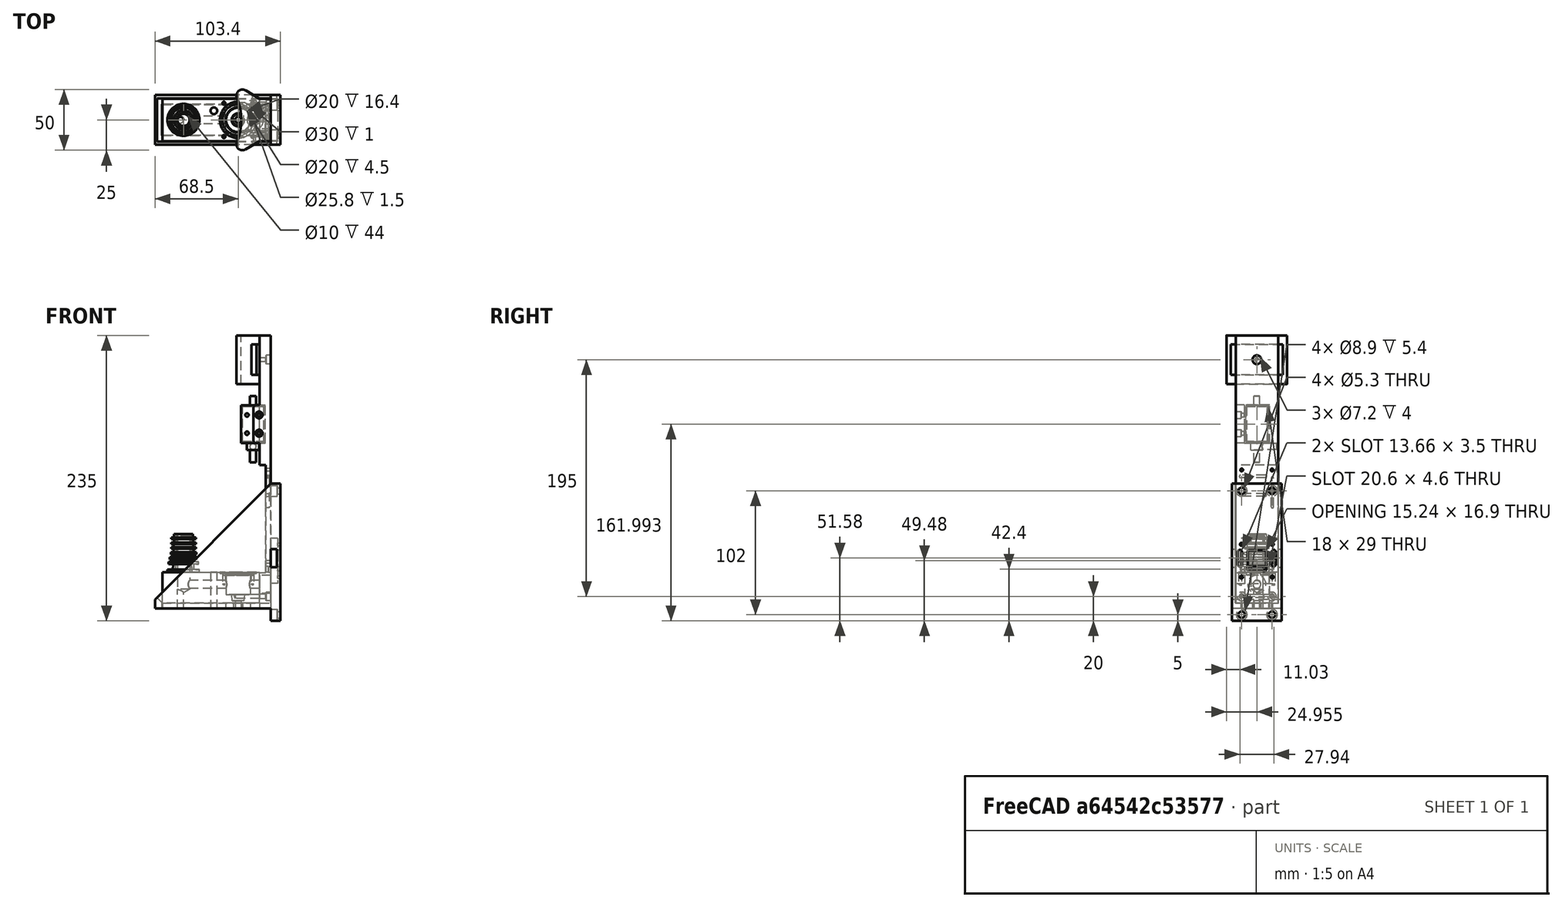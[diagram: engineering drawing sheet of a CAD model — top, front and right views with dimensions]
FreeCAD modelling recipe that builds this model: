
FCSTD DOCUMENT  (FreeCAD 1.0R39109 (Git))
Label: Bottle Nozzle V6.1
License: All rights reserved
LicenseURL: http://en.wikipedia.org/wiki/All_rights_reserved
objects: Sketcher::SketchObject×31, PartDesign::Pocket×12, PartDesign::Hole×10, PartDesign::Pad×6, Mesh::Feature×5, PartDesign::Body×4, TechDraw::DrawProjGroupItem×3, TechDraw::DrawViewDimension×3, PartDesign::Revolution×2, Spreadsheet::Sheet×1, PartDesign::Groove×1, TechDraw::DrawSVGTemplate×1, TechDraw::DrawPage×1, Part::FeaturePython×1
note: 160 computed .brp shape members not serialized (recipe doc carries the construction recipe); baked Part::Feature solids carry a one-line shape summary decoded from their .brp

FEATURE [Sketcher::SketchObject] Sketch
  ArcFitTolerance = 0
  FullyConstrained = true
  MakeInternals = false
  MapMode = 5
  Placement = pos=(0,0,0) rot=(1,0,0;1.5708rad)
  expr: Constraints[10] = Spreadsheet.HeightPart
  expr: Constraints[12] = Spreadsheet.PartWidth / 2
  expr: Constraints[13] = Spreadsheet.PipeCircle / 2
  expr: Constraints[17] = Spreadsheet.HeigthDop
  expr: Constraints[8] = Spreadsheet.PartWidth2 / 2
  sketch-geometry (8):
    g0: LineSegment StartX=6 StartY=60 StartZ=0 EndX=6.75 EndY=30 EndZ=0
    g1: LineSegment [constr] StartX=6.75 StartY=30 StartZ=0 EndX=17.5 EndY=30 EndZ=0
    g2: LineSegment [constr] StartX=17.5 StartY=30 StartZ=0 EndX=17.5 EndY=0 EndZ=0
    g3: LineSegment [constr] StartX=17.5 StartY=0 StartZ=0 EndX=0 EndY=0 EndZ=0
    g4: LineSegment StartX=0 StartY=60 StartZ=0 EndX=6 EndY=60 EndZ=0
    g5: LineSegment [constr] StartX=0 StartY=60 StartZ=0 EndX=0 EndY=0 EndZ=0
    g6: LineSegment StartX=6.75 StartY=30 StartZ=0 EndX=0 EndY=30 EndZ=0
    g7: LineSegment StartX=0 StartY=30 StartZ=0 EndX=0 EndY=60 EndZ=0
  constraints (23):
    c: Coincident(g0,g1)
    c: Coincident(g1,g2)
    c: Vertical(g2)
    c: Coincident(g2,g3)
    c: Horizontal(g3)
    c: Coincident(g4,g0)
    c: Horizontal(g4)
    c: Horizontal(g1)
    c: DistanceX(g-1,g0) = 6.75
    c: Coincident(g5,g4)
    c: DistanceY(g2,g2) = 30
    c: Vertical(g5)
    c: DistanceX(g-1,g0) = 6
    c: DistanceX(g-1,g2) = 17.5
    c: Coincident(g3,g5)
    c: PointOnObject(g-1,g3)
    c: PointOnObject(g-1,g5)
    c: DistanceY(g1,g0) = 30
    c: Coincident(g6,g0)
    c: PointOnObject(g6,g5)
    c: Horizontal(g6)
    c: Coincident(g7,g6)
    c: Coincident(g7,g4)
FEATURE [PartDesign::Revolution] Revolution
  Angle = 360
  Angle2 = 60
  Axis = (0,2e-16,1)
  Base = (0,0,0)
  Placement = pos=(0,0,0) rot=(1,0,0;1.5708rad)
  Profile = -> Sketch
  ReferenceAxis = -> Sketch [V_Axis]
  Reversed = true
  Suppressed = false
  Type = 0
FEATURE [Spreadsheet::Sheet] Spreadsheet
  cells = A1='DiameterTube; B1(DiameterTube)==5 mm; C1==(B1 / 2) ^ 2 * pi; E1='Outer available; F1==C4 - C1; G1='Similair to inner tube; H1==sqrt(F1 / pi); A2='TubeOffset; B2(TubeOffset)==2.5 mm; C2==(HeightPart - DiameterTube) / 2; A3='DiameterTubeInner; B3(DiameterTubeInner)==B1 - 2 mm; C3==(B3 / 2) ^ 2 * pi; E3='Inner available; F3==C3; H3==sqrt(F3 / pi); A4='DiameterHole; B4(DiameterHole)==10 mm; C4==(B4 / 2) ^ 2 * pi; D4='Max = PartWidth-Walls*2; E4='Ratio liquid VS air surface; F4==F1 / F3; A5='PipeCircle; B5(PipeCircle)==35 mm; A6='HeightPart; B6(HeightPart)==30 mm; A7='HeigthDop; B7(HeigthDop)==30 mm; A8='PartWidth; B8(PartWidth)==12 mm; A9='PartWidth2; B9(PartWidth2)==13.5 mm; A10='MountingHoleDistance; B10(MountingHoleDistance)==round(sqrt((((PipeCircle - PartWidth2) / 2 + PartWidth2) / 2) ^ 2 * 2) / 2.5) * 2.5; A11='OffsetFluidHole2; B11(OffsetFluidHole2)==OffsetFlakte - (4 mm + 0.8 mm * 8 / 2); C11='Blindstop Depth is 3mm+1mm spacer, M5 = 4.2mm; A12='WidthFlank; B12(WidthFlank)==10 mm; A13='OffsetFlakte; B13(OffsetFlakte)==sqrt(PipeCircle ^ 2 - (WidthFlank / 2) ^ 2) / 2 - 0.82 mm; A14='FluidHole; B14(FluidHole)==5 mm; C14='M7; A15='FluidHoleOutsideTube; B15(FluidHoleOutsideTube)==FluidHole + 2 mm; A16='PartOffset; B16(PartOffset)=10; A17='offsetvalve; B17(offsetvalve)=45
FEATURE [Sketcher::SketchObject] Sketch003
  ArcFitTolerance = 0
  AttachmentOffset = pos=(0,0,60) rot=(0,0,1;0rad)
  FullyConstrained = true
  MakeInternals = false
  MapMode = 5
  Placement = pos=(0,0,60) rot=(0,0,1;0rad)
  expr: .AttachmentOffset.Base.z = Spreadsheet.HeightPart + Spreadsheet.HeigthDop
  expr: Constraints[1] = Spreadsheet.DiameterHole
  sketch-geometry (1):
    g0: Circle CenterX=0 CenterY=0 CenterZ=0 NormalX=0 NormalY=0 NormalZ=1 AngleXU=0 Radius=5
  constraints (2):
    c: Coincident(g0,g-1)
    c: Diameter(g0) = 10
FEATURE [Sketcher::SketchObject] Sketch005
  ArcFitTolerance = 0
  FullyConstrained = true
  MakeInternals = false
  MapMode = 5
  expr: Constraints[0] = Spreadsheet.DiameterTube
  expr: Constraints[2] = Spreadsheet.TubeOffset
  sketch-geometry (1):
    g0: Circle CenterX=-2.5 CenterY=0 CenterZ=0 NormalX=0 NormalY=0 NormalZ=1 AngleXU=0 Radius=2.5
  constraints (3):
    c: Diameter(g0) = 5
    c: PointOnObject(g0,g-1)
    c: DistanceX(g0,g-1) = 2.5
FEATURE [Sketcher::SketchObject] Sketch006
  ArcFitTolerance = 0
  FullyConstrained = true
  MakeInternals = false
  MapMode = 5
  expr: Constraints[18] = Spreadsheet.PipeCircle / 2
  expr: Constraints[9] = Spreadsheet.PipeCircle
  sketch-geometry (7):
    g0: LineSegment StartX=0 StartY=17.5 StartZ=0 EndX=62.5 EndY=17.5 EndZ=0
    g1: LineSegment StartX=62.5 StartY=17.5 StartZ=0 EndX=62.5 EndY=-17.5 EndZ=0
    g2: LineSegment StartX=62.5 StartY=-17.5 StartZ=0 EndX=0 EndY=-17.5 EndZ=0
    g3: LineSegment [constr] StartX=0 StartY=-17.5 StartZ=0 EndX=0 EndY=17.5 EndZ=0
    g4: LineSegment StartX=0 StartY=17.5 StartZ=0 EndX=-17.5 EndY=17.5 EndZ=0
    g5: LineSegment StartX=-17.5 StartY=17.5 StartZ=0 EndX=-17.5 EndY=-17.5 EndZ=0
    g6: LineSegment StartX=-17.5 StartY=-17.5 StartZ=0 EndX=0 EndY=-17.5 EndZ=0
  constraints (19):
    c: Coincident(g0,g1)
    c: Coincident(g1,g2)
    c: Coincident(g2,g3)
    c: Coincident(g3,g0)
    c: Horizontal(g0)
    c: Horizontal(g2)
    c: Vertical(g1)
    c: PointOnObject(g0,g-2)
    c: Symmetric(g0,g2,g-1)
    c: DistanceY(g3,g3) = 35
    c: DistanceX(g0,g0) = 62.5  'ww'
    c: Coincident(g0,g4)
    c: Horizontal(g4)
    c: Coincident(g4,g5)
    c: Vertical(g5)
    c: Coincident(g5,g6)
    c: Coincident(g6,g2)
    c: Horizontal(g6)
    c: DistanceX(g4,g4) = 17.5
FEATURE [PartDesign::Pad] Pad
  BaseFeature = -> Revolution
  Direction = (0,0,1)
  Length = 30
  Length2 = 10
  Placement = pos=(0,0,0) rot=(1,0,0;1.5708rad)
  Profile = -> Sketch006
  ReferenceAxis = -> Sketch006 [N_Axis]
  Suppressed = false
  Type = 0
  expr: Length = Spreadsheet.HeightPart
FEATURE [PartDesign::Hole] Hole  label="Hole Combination"
  BaseFeature = -> Pad
  CustomThreadClearance = 0
  Depth = 44
  DepthType = 0
  Diameter = 10
  DrillForDepth = false
  DrillPoint = 1
  DrillPointAngle = 118
  HoleCutCountersinkAngle = 90
  HoleCutCustomValues = false
  HoleCutDepth = 0
  HoleCutDiameter = 10.1
  HoleCutType = 0
  ModelThread = false
  Placement = pos=(0,0,0) rot=(1,0,0;1.5708rad)
  Profile = -> Sketch003
  Suppressed = false
  Tapered = false
  TaperedAngle = 90
  ThreadClass = 0
  ThreadDepth = 44
  ThreadDepthType = 0
  ThreadDirection = 0
  ThreadFit = 0
  ThreadSize = 0
  ThreadType = 0
  Threaded = false
  UseCustomThreadClearance = false
  expr: Depth = 44 mm
FEATURE [PartDesign::Hole] Hole001  label="Hole Air"
  BaseFeature = -> Hole
  CustomThreadClearance = 0
  Depth = 210.228
  DepthType = 1
  Diameter = 5
  DrillForDepth = false
  DrillPoint = 1
  DrillPointAngle = 118
  HoleCutCountersinkAngle = 90
  HoleCutCustomValues = false
  HoleCutDepth = 0
  HoleCutDiameter = 6.1
  HoleCutType = 0
  ModelThread = false
  Placement = pos=(0,0,0) rot=(1,0,0;1.5708rad)
  Profile = -> Sketch005
  Reversed = true
  Suppressed = false
  Tapered = false
  TaperedAngle = 90
  ThreadClass = 0
  ThreadDepth = 210.228
  ThreadDepthType = 0
  ThreadDirection = 0
  ThreadFit = 0
  ThreadSize = 0
  ThreadType = 0
  Threaded = false
  UseCustomThreadClearance = false
FEATURE [Sketcher::SketchObject] Sketch011
  ArcFitTolerance = 0
  AttachmentOffset = pos=(0,0,62.5) rot=(0,0,1;0rad)
  FullyConstrained = true
  MakeInternals = false
  MapMode = 5
  Placement = pos=(62.5,0,0) rot=(0.57735,0.57735,0.57735;2.0944rad)
  expr: .AttachmentOffset.Base.z = Sketch006.Constraints.ww
  expr: .Constraints.hh = 20
  sketch-geometry (1):
    g0: Circle CenterX=0 CenterY=20 CenterZ=0 NormalX=0 NormalY=0 NormalZ=1 AngleXU=0 Radius=4
  constraints (3):
    c: PointOnObject(g0,g-2)
    c: Diameter(g0) = 8
    c: DistanceY(g-1,g0) = 20  'hh'
FEATURE [PartDesign::Hole] Hole002  label="Hole Side"
  BaseFeature = -> Hole001
  CustomThreadClearance = 0
  Depth = 60
  DepthType = 0
  Diameter = 6.4
  DrillForDepth = false
  DrillPoint = 1
  DrillPointAngle = 118
  HoleCutCountersinkAngle = 90
  HoleCutCustomValues = false
  HoleCutDepth = 0
  HoleCutDiameter = 0
  HoleCutType = 0
  ModelThread = false
  Placement = pos=(0,0,0) rot=(1,0,0;1.5708rad)
  Profile = -> Sketch011
  Suppressed = false
  Tapered = false
  TaperedAngle = 90
  ThreadClass = 0
  ThreadDepth = 60
  ThreadDepthType = 0
  ThreadDirection = 0
  ThreadFit = 0
  ThreadSize = 0
  ThreadType = 0
  Threaded = false
  UseCustomThreadClearance = false
  expr: Diameter = 8 * 0.8
FEATURE [Sketcher::SketchObject] Sketch012
  ArcFitTolerance = 0
  AttachmentOffset = pos=(0,0,45) rot=(0,0,1;0rad)
  FullyConstrained = true
  MakeInternals = false
  MapMode = 5
  Placement = pos=(45,0,0) rot=(0.57735,0.57735,0.57735;2.0944rad)
  expr: .AttachmentOffset.Base.z = Spreadsheet.offsetvalve
  expr: Constraints[13] = 25.8 / 2
  expr: Constraints[17] = 20 / 2
  expr: Constraints[24] = 10.8 / 2
  expr: Constraints[25] = 8.6 / 2
  sketch-geometry (15):
    g0: LineSegment StartX=15 StartY=30 StartZ=0 EndX=15 EndY=29 EndZ=0
    g1: LineSegment StartX=15 StartY=29 StartZ=0 EndX=12.9 EndY=29 EndZ=0
    g2: LineSegment StartX=12.9 StartY=29 StartZ=0 EndX=12.9 EndY=27.5 EndZ=0
    g3: LineSegment StartX=12.9 StartY=27.5 StartZ=0 EndX=10.4 EndY=27.5 EndZ=0
    g4: LineSegment StartX=10.4 StartY=27.5 StartZ=0 EndX=10.4 EndY=27.9 EndZ=0
    g5: LineSegment StartX=10 StartY=27.9 StartZ=0 EndX=10 EndY=11.5 EndZ=0
    g6: LineSegment StartX=10 StartY=27.9 StartZ=0 EndX=10.4 EndY=27.9 EndZ=0
    g7: LineSegment StartX=10 StartY=11.5 StartZ=0 EndX=5.4 EndY=11.5 EndZ=0
    g8: LineSegment [constr] StartX=5.4 StartY=11.5 StartZ=0 EndX=4.3 EndY=2.5 EndZ=0
    g9: LineSegment StartX=0 StartY=30 StartZ=0 EndX=0 EndY=0 EndZ=0
    g10: LineSegment StartX=15 StartY=30 StartZ=0 EndX=0 EndY=30 EndZ=0
    g11: LineSegment StartX=2.5 StartY=6.5 StartZ=0 EndX=2.5 EndY=0 EndZ=0
    g12: LineSegment StartX=0 StartY=0 StartZ=0 EndX=2.5 EndY=0 EndZ=0
    g13: LineSegment StartX=5.4 StartY=11.5 StartZ=0 EndX=4.78889 EndY=6.5 EndZ=0
    g14: LineSegment StartX=4.78889 StartY=6.5 StartZ=0 EndX=2.5 EndY=6.5 EndZ=0
  constraints (45):
    c: Vertical(g0)
    c: DistanceY(g-1,g0) = 30
    c: Coincident(g0,g1)
    c: Horizontal(g1)
    c: Coincident(g1,g2)
    c: Vertical(g2)
    c: Coincident(g2,g3)
    c: Coincident(g3,g4)
    c: Vertical(g4)
    c: Vertical(g5)
    c: Horizontal(g3)
    c: DistanceY(g0,g0) = 1
    c: DistanceY(g2,g2) = 1.5
    c: DistanceX(g-1,g1) = 12.9
    c: Coincident(g6,g5)
    c: Coincident(g6,g4)
    c: Horizontal(g6)
    c: DistanceX(g-1,g5) = 10
    c: DistanceY(g4,g4) = 0.4
    c: Equal(g4,g6)
    c: Coincident(g5,g7)
    c: Coincident(g7,g8)
    c: PointOnObject(g9,g-2)
    c: Horizontal(g7)
    c: DistanceX(g-1,g7) = 5.4
    c: DistanceX(g-1,g8) = 4.3
    c: DistanceY(g8,g8) = 9
    c: DistanceY(g5,g3) = 16
    c: DistanceX(g-1,g0) = 15
    c: Coincident(g10,g0)
    c: Coincident(g10,g9)
    c: Horizontal(g10)
    c: DistanceX(g9,g11) = 2.5
    c: PointOnObject(g9,g-2)
    c: PointOnObject(g9,g-1)
    c: PointOnObject(g11,g-1)
    c: Vertical(g11)
    c: Coincident(g12,g9)
    c: Coincident(g12,g11)
    c: Coincident(g13,g7)
    c: PointOnObject(g13,g8)
    c: Coincident(g14,g13)
    c: Horizontal(g14)
    c: DistanceY(g13,g13) = 5
    c: Coincident(g11,g14)
FEATURE [PartDesign::Groove] Groove  label="Groove valve"
  Angle = 360
  Angle2 = 60
  Axis = (1e-16,-1e-16,1)
  Base = (45,0,0)
  BaseFeature = -> Hole002
  Placement = pos=(0,0,0) rot=(1,0,0;1.5708rad)
  Profile = -> Sketch012
  ReferenceAxis = -> Sketch012 [V_Axis]
  Suppressed = false
  Type = 0
FEATURE [Sketcher::SketchObject] Sketch013
  ArcFitTolerance = 0
  AttachmentOffset = pos=(0,0,30) rot=(0,0,1;0rad)
  FullyConstrained = true
  MakeInternals = false
  MapMode = 5
  Placement = pos=(0,0,30) rot=(0,0,1;0rad)
  expr: .AttachmentOffset.Base.z = Spreadsheet.HeightPart
  expr: Constraints[10] = Spreadsheet.offsetvalve
  sketch-geometry (9):
    g0: LineSegment [constr] StartX=33.25 StartY=-13.75 StartZ=0 EndX=33.25 EndY=13.75 EndZ=0
    g1: LineSegment [constr] StartX=33.25 StartY=13.75 StartZ=0 EndX=56.75 EndY=13.75 EndZ=0
    g2: LineSegment [constr] StartX=56.75 StartY=13.75 StartZ=0 EndX=56.75 EndY=-13.75 EndZ=0
    g3: LineSegment [constr] StartX=56.75 StartY=-13.75 StartZ=0 EndX=33.25 EndY=-13.75 EndZ=0
    g4: GeomPoint X=45 Y=-6e-16 Z=0
    g5: Circle CenterX=33.25 CenterY=13.75 CenterZ=0 NormalX=0 NormalY=0 NormalZ=1 AngleXU=0 Radius=1.75
    g6: Circle CenterX=56.75 CenterY=13.75 CenterZ=0 NormalX=0 NormalY=0 NormalZ=1 AngleXU=0 Radius=1.75
    g7: Circle CenterX=33.25 CenterY=-13.75 CenterZ=0 NormalX=0 NormalY=0 NormalZ=1 AngleXU=0 Radius=1.75
    g8: Circle CenterX=56.75 CenterY=-13.75 CenterZ=0 NormalX=0 NormalY=0 NormalZ=1 AngleXU=0 Radius=1.75
  constraints (21):
    c: Coincident(g0,g1)
    c: Coincident(g1,g2)
    c: Coincident(g2,g3)
    c: Coincident(g3,g0)
    c: Horizontal(g1)
    c: Horizontal(g3)
    c: Vertical(g0)
    c: Vertical(g2)
    c: Symmetric(g1,g0,g4)
    c: PointOnObject(g4,g-1)
    c: DistanceX(g-1,g4) = 45
    c: Coincident(g5,g0)
    c: DistanceX(g1,g1) = 23.5
    c: DistanceY(g2,g2) = 27.5
    c: Coincident(g6,g1)
    c: Coincident(g7,g0)
    c: Coincident(g8,g2)
    c: Equal(g5,g6)
    c: Equal(g6,g7)
    c: Equal(g7,g8)
    c: Diameter(g6) = 3.5
FEATURE [PartDesign::Hole] Hole003  label="Hole mouting valve thread"
  BaseFeature = -> Groove
  CustomThreadClearance = 0
  Depth = 10
  DepthType = 0
  Diameter = 2.5
  DrillForDepth = false
  DrillPoint = 1
  DrillPointAngle = 118
  HoleCutCountersinkAngle = 90
  HoleCutCustomValues = false
  HoleCutDepth = 0
  HoleCutDiameter = 6.1
  HoleCutType = 0
  ModelThread = false
  Placement = pos=(0,0,0) rot=(1,0,0;1.5708rad)
  Profile = -> Sketch013
  Suppressed = false
  Tapered = false
  TaperedAngle = 90
  ThreadClass = 0
  ThreadDepth = 10
  ThreadDepthType = 0
  ThreadDirection = 0
  ThreadFit = 0
  ThreadSize = 9
  ThreadType = 1
  Threaded = true
  UseCustomThreadClearance = false
FEATURE [Sketcher::SketchObject] Sketch014
  ArcFitTolerance = 0
  AttachmentOffset = pos=(0,0,62.5) rot=(0,0,1;0rad)
  FullyConstrained = false
  MakeInternals = false
  MapMode = 5
  Placement = pos=(62.5,0,0) rot=(0.57735,0.57735,0.57735;2.0944rad)
  expr: .AttachmentOffset.Base.z = Sketch006.Constraints.ww
  expr: Constraints[1] = Sketch011.Constraints.hh
  sketch-geometry (1):
    g0: Circle CenterX=0 CenterY=20 CenterZ=0 NormalX=0 NormalY=0 NormalZ=1 AngleXU=0 Radius=3.71689
  constraints (2):
    c: PointOnObject(g0,g-2)
    c: DistanceY(g-1,g0) = 20
FEATURE [PartDesign::Hole] Hole004  label="Hole Side thread"
  BaseFeature = -> Hole003
  CustomThreadClearance = 0
  Depth = 20
  DepthType = 0
  Diameter = 6.8
  DrillForDepth = false
  DrillPoint = 1
  DrillPointAngle = 118
  HoleCutCountersinkAngle = 90
  HoleCutCustomValues = false
  HoleCutDepth = 0
  HoleCutDiameter = 6.1
  HoleCutType = 0
  ModelThread = false
  Placement = pos=(0,0,0) rot=(1,0,0;1.5708rad)
  Profile = -> Sketch014
  Suppressed = false
  Tapered = false
  TaperedAngle = 90
  ThreadClass = 0
  ThreadDepth = 20
  ThreadDepthType = 0
  ThreadDirection = 0
  ThreadFit = 0
  ThreadSize = 16
  ThreadType = 1
  Threaded = true
  UseCustomThreadClearance = false
FEATURE [Sketcher::SketchObject] Sketch015
  ArcFitTolerance = 0
  AttachmentOffset = pos=(0,0,4.5) rot=(0,0,1;0rad)
  FullyConstrained = true
  MakeInternals = false
  MapMode = 5
  Placement = pos=(0,0,4.5) rot=(0,0,1;0rad)
  expr: Constraints[14] = Spreadsheet.PipeCircle
  expr: Constraints[15] = Sketch006.Constraints.ww
  expr: Constraints[2] = Spreadsheet.offsetvalve
  sketch-geometry (14):
    g0: Circle CenterX=45 CenterY=0 CenterZ=0 NormalX=0 NormalY=0 NormalZ=1 AngleXU=0 Radius=10
    g1: Circle CenterX=45 CenterY=0 CenterZ=0 NormalX=0 NormalY=0 NormalZ=1 AngleXU=0 Radius=3.5
    g2: LineSegment [constr] StartX=0 StartY=17.5 StartZ=0 EndX=62.5 EndY=17.5 EndZ=0
    g3: LineSegment [constr] StartX=62.5 StartY=17.5 StartZ=0 EndX=62.5 EndY=-17.5 EndZ=0
    g4: LineSegment [constr] StartX=62.5 StartY=-17.5 StartZ=0 EndX=0 EndY=-17.5 EndZ=0
    g5: LineSegment [constr] StartX=0 StartY=-17.5 StartZ=0 EndX=0 EndY=17.5 EndZ=0
    g6: LineSegment StartX=62.5 StartY=17.5 StartZ=0 EndX=-50 EndY=17.5 EndZ=0
    g7: LineSegment StartX=-50 StartY=17.5 StartZ=0 EndX=-50 EndY=12.5 EndZ=0
    g8: LineSegment StartX=-50 StartY=12.5 StartZ=0 EndX=62.5 EndY=12.5 EndZ=0
    g9: LineSegment StartX=62.5 StartY=12.5 StartZ=0 EndX=62.5 EndY=17.5 EndZ=0
    g10: LineSegment StartX=62.5 StartY=-17.5 StartZ=0 EndX=-50 EndY=-17.5 EndZ=0
    g11: LineSegment StartX=-50 StartY=-17.5 StartZ=0 EndX=-50 EndY=-12.5 EndZ=0
    g12: LineSegment StartX=-50 StartY=-12.5 StartZ=0 EndX=62.5 EndY=-12.5 EndZ=0
    g13: LineSegment StartX=62.5 StartY=-12.5 StartZ=0 EndX=62.5 EndY=-17.5 EndZ=0
  constraints (38):
    c: PointOnObject(g0,g-1)
    c: Coincident(g1,g0)
    c: DistanceX(g-1,g0) = 45
    c: Diameter(g1) = 7
    c: Diameter(g0) = 20
    c: Coincident(g2,g3)
    c: Coincident(g3,g4)
    c: Coincident(g4,g5)
    c: Coincident(g5,g2)
    c: Horizontal(g2)
    c: Horizontal(g4)
    c: Vertical(g5)
    c: PointOnObject(g2,g-2)
    c: Symmetric(g2,g3,g-1)
    c: DistanceY(g3,g3) = 35
    c: DistanceX(g2,g2) = 62.5
    c: Coincident(g6,g7)
    c: Coincident(g7,g8)
    c: Coincident(g8,g9)
    c: Coincident(g9,g6)
    c: Horizontal(g6)
    c: Horizontal(g8)
    c: Vertical(g7)
    c: Vertical(g9)
    c: Coincident(g6,g2)
    c: Coincident(g10,g11)
    c: Coincident(g11,g12)
    c: Coincident(g12,g13)
    c: Coincident(g13,g10)
    c: Horizontal(g10)
    c: Horizontal(g12)
    c: Vertical(g11)
    c: Vertical(g13)
    c: Coincident(g10,g3)
    c: Vertical(g11,g7)
    c: DistanceY(g12,g8) = 25
    c: Equal(g7,g11)
    c: DistanceX(g6,g2) = 50
FEATURE [PartDesign::Pocket] Pocket001  label="Pocket fluid outlet pipe"
  BaseFeature = -> Hole004
  Direction = (0,0,-1)
  Length = 5
  Length2 = 5
  Placement = pos=(0,0,0) rot=(1,0,0;1.5708rad)
  Profile = -> Sketch015
  ReferenceAxis = -> Sketch015 [N_Axis]
  Suppressed = false
  Type = 0
FEATURE [Sketcher::SketchObject] Sketch016
  ArcFitTolerance = 0
  AttachmentOffset = pos=(0,0,62.5) rot=(0,0,1;0rad)
  FullyConstrained = false
  MakeInternals = false
  MapMode = 5
  Placement = pos=(62.5,0,0) rot=(0.57735,0.57735,0.57735;2.0944rad)
  sketch-geometry (9):
    g0: LineSegment [constr] StartX=-12.5 StartY=10 StartZ=0 EndX=12.5 EndY=10 EndZ=0
    g1: LineSegment [constr] StartX=12.5 StartY=10 StartZ=0 EndX=12.5 EndY=25 EndZ=0
    g2: LineSegment [constr] StartX=12.5 StartY=25 StartZ=0 EndX=-12.5 EndY=25 EndZ=0
    g3: LineSegment [constr] StartX=-12.5 StartY=25 StartZ=0 EndX=-12.5 EndY=10 EndZ=0
    g4: GeomPoint [constr] X=0 Y=17.5 Z=0
    g5: Circle [constr] CenterX=12.5 CenterY=25 CenterZ=0 NormalX=0 NormalY=0 NormalZ=1 AngleXU=0 Radius=2.9952
    g6: Circle [constr] CenterX=-12.5 CenterY=25 CenterZ=0 NormalX=0 NormalY=0 NormalZ=1 AngleXU=0 Radius=2.9952
    g7: Circle CenterX=-12.5 CenterY=10 CenterZ=0 NormalX=0 NormalY=0 NormalZ=1 AngleXU=0 Radius=2.9952
    g8: Circle CenterX=12.5 CenterY=10 CenterZ=0 NormalX=0 NormalY=0 NormalZ=1 AngleXU=0 Radius=2.9952
  constraints (20):
    c: Coincident(g0,g1)
    c: Coincident(g1,g2)
    c: Coincident(g2,g3)
    c: Coincident(g3,g0)
    c: Horizontal(g0)
    c: Horizontal(g2)
    c: Vertical(g1)
    c: Vertical(g3)
    c: Symmetric(g2,g0,g4)
    c: PointOnObject(g4,g-2)
    c: DistanceX(g2,g2) = 25
    c: DistanceY(g1,g1) = 15
    c: Coincident(g5,g1)
    c: Coincident(g6,g2)
    c: Coincident(g7,g0)
    c: Coincident(g8,g0)
    c: Equal(g5,g8)
    c: Equal(g8,g7)
    c: Equal(g7,g6)
    c: DistanceY(g-1,g0) = 10
FEATURE [PartDesign::Hole] Hole005  label="Hole bottle holder mounting"
  BaseFeature = -> Pocket001
  CustomThreadClearance = 0
  Depth = 20
  DepthType = 0
  Diameter = 3.2
  DrillForDepth = false
  DrillPoint = 1
  DrillPointAngle = 118
  HoleCutCountersinkAngle = 90
  HoleCutCustomValues = false
  HoleCutDepth = 0
  HoleCutDiameter = 6.1
  HoleCutType = 0
  ModelThread = false
  Placement = pos=(0,0,0) rot=(1,0,0;1.5708rad)
  Profile = -> Sketch016
  Refine = true
  Suppressed = false
  Tapered = false
  TaperedAngle = 90
  ThreadClass = 0
  ThreadDepth = 20
  ThreadDepthType = 0
  ThreadDirection = 0
  ThreadFit = 0
  ThreadSize = 0
  ThreadType = 0
  Threaded = false
  UseCustomThreadClearance = false
  expr: Diameter = 0.8 * 4
FEATURE [Sketcher::SketchObject] Sketch018
  ArcFitTolerance = 0
  FullyConstrained = true
  MakeInternals = false
  MapMode = 5
  Placement = pos=(0,0,0) rot=(1,0,0;1.5708rad)
  expr: .Constraints.width = 71.9
  sketch-geometry (15):
    g0: LineSegment StartX=71.9 StartY=102.9 StartZ=0 EndX=-23.5 EndY=7.5 EndZ=0
    g1: LineSegment StartX=-23.5 StartY=7.5 StartZ=0 EndX=-23.5 EndY=0 EndZ=0
    g2: LineSegment StartX=-23.5 StartY=0 StartZ=0 EndX=71.9 EndY=0 EndZ=0
    g3: LineSegment [constr] StartX=71.9 StartY=0 StartZ=0 EndX=71.9 EndY=102.9 EndZ=0
    g4: LineSegment StartX=71.9 StartY=0 StartZ=0 EndX=71.9 EndY=-10 EndZ=0
    g5: Circle [constr] CenterX=-20.7041 CenterY=3.75 CenterZ=0 NormalX=0 NormalY=0 NormalZ=1 AngleXU=0 Radius=1.6
    g6: LineSegment [constr] StartX=-23.5 StartY=7.5 StartZ=0 EndX=-20.5 EndY=7.5 EndZ=0
    g7: LineSegment [constr] StartX=-20.5 StartY=7.5 StartZ=0 EndX=-17.5 EndY=4.5 EndZ=0
    g8: LineSegment [constr] StartX=-23.5 StartY=0 StartZ=0 EndX=-20.7041 EndY=3.75 EndZ=0
    g9: LineSegment [constr] StartX=-20.7041 StartY=3.75 StartZ=0 EndX=-23.5 EndY=7.5 EndZ=0
    g10: LineSegment [constr] StartX=-23.5 StartY=3.75 StartZ=0 EndX=-22.3041 EndY=3.75 EndZ=0
    g11: LineSegment [constr] StartX=-18.727 StartY=5.72703 StartZ=0 EndX=-19.5727 EndY=4.88137 EndZ=0
    g12: LineSegment StartX=71.9 StartY=102.9 StartZ=0 EndX=79.9 EndY=102.9 EndZ=0
    g13: LineSegment StartX=79.9 StartY=102.9 StartZ=0 EndX=79.9 EndY=-10 EndZ=0
    g14: LineSegment StartX=71.9 StartY=-10 StartZ=0 EndX=79.9 EndY=-10 EndZ=0
  constraints (45):
    c: Coincident(g0,g1)
    c: Coincident(g1,g2)
    c: PointOnObject(g3,g-1)
    c: Vertical(g3)
    c: Vertical(g4)
    c: DistanceX(g1,g-1) = 23.5
    c: DistanceY(g1,g1) = 7.5
    c: DistanceX(g-1,g3) = 71.9  'width'
    c: PointOnObject(g-1,g2)
    c: Horizontal(g2)
    c: Vertical(g1)
    c: Coincident(g4,g2)
    c: Vertical(g0,g2)
    c: Angle(g2,g0) = 0.785398
    c: DistanceY(g4,g4) = 10  'MountingHeight'
    c: Diameter(g5) = 3.2
    c: Coincident(g6,g0)
    c: Horizontal(g6)
    c: Coincident(g7,g6)
    c: DistanceX(g6,g6) = 3
    c: DistanceX(g7,g7) = 3
    c: DistanceY(g7,g7) = 3
    c: Coincident(g8,g1)
    c: Coincident(g8,g5)
    c: Coincident(g9,g5)
    c: Coincident(g9,g0)
    c: Equal(g9,g8)
    c: PointOnObject(g10,g1)
    c: PointOnObject(g10,g5)
    c: Horizontal(g10)
    c: PointOnObject(g11,g7)
    c: PointOnObject(g11,g5)
    c: Perpendicular(g7,g11)
    c: Equal(g10,g11)
    c: PointOnObject(g5,g10)
    c: PointOnObject(g5,g11)
    c: Horizontal(g12)
    c: Distance(g12,g12) = 8
    c: Coincident(g12,g13)
    c: Vertical(g13)
    c: Coincident(g14,g4)
    c: Coincident(g14,g13)
    c: Horizontal(g14)
    c: Coincident(g0,g12)
    c: Coincident(g3,g0)
FEATURE [PartDesign::Pad] Pad001  label="Pad all"
  Direction = (0,-1,2e-16)
  Length = 41
  Length2 = 10
  Midplane = true
  Placement = pos=(0,0,0) rot=(1,0,0;1.5708rad)
  Profile = -> Sketch018
  ReferenceAxis = -> Sketch018 [N_Axis]
  Suppressed = false
  Type = 0
  expr: Length = 35 + 3 * 2
FEATURE [Sketcher::SketchObject] Sketch019
  ArcFitTolerance = 0
  FullyConstrained = true
  MakeInternals = false
  MapMode = 5
  Placement = pos=(0,0,0) rot=(1,0,0;1.5708rad)
  expr: Constraints[3] = Sketch018.Constraints.width
  sketch-geometry (5):
    g0: LineSegment StartX=-17.5 StartY=4.5 StartZ=0 EndX=71.9 EndY=4.5 EndZ=0
    g1: LineSegment StartX=71.9 StartY=4.5 StartZ=0 EndX=71.9 EndY=104.5 EndZ=0
    g2: LineSegment StartX=-17.5 StartY=4.5 StartZ=0 EndX=-27.5 EndY=14.5 EndZ=0
    g3: LineSegment StartX=-27.5 StartY=14.5 StartZ=0 EndX=-27.5 EndY=104.5 EndZ=0
    g4: LineSegment StartX=-27.5 StartY=104.5 StartZ=0 EndX=71.9 EndY=104.5 EndZ=0
  constraints (15):
    c: Horizontal(g0)
    c: Coincident(g0,g1)
    c: Vertical(g1)
    c: DistanceX(g-1,g1) = 71.9
    c: DistanceY(g-1,g0) = 4.5
    c: Coincident(g3,g2)
    c: Vertical(g3)
    c: DistanceX(g0,g-1) = 17.5
    c: Coincident(g4,g3)
    c: Coincident(g4,g1)
    c: Horizontal(g4)
    c: Angle(g0,g2) = 2.35619
    c: Coincident(g2,g0)
    c: DistanceX(g2,g2) = 10
    c: DistanceY(g1,g1) = 100
FEATURE [PartDesign::Pocket] Pocket  label="Pocket 1"
  BaseFeature = -> Pad001
  Direction = (0,1,-2e-16)
  Length = 35.6
  Length2 = 5
  Midplane = true
  Placement = pos=(0,0,0) rot=(1,0,0;1.5708rad)
  Profile = -> Sketch019
  ReferenceAxis = -> Sketch019 [N_Axis]
  Suppressed = false
  Type = 0
  expr: Length = 35 + 0.6
FEATURE [Sketcher::SketchObject] Sketch020
  ArcFitTolerance = 0
  FullyConstrained = true
  MakeInternals = false
  MapMode = 5
  Placement = pos=(0,0,0) rot=(1,0,0;1.5708rad)
  expr: Constraints[10] = 17.5 mm + 0.25 mm
  expr: Constraints[11] = Sketch018.Constraints.width
  sketch-geometry (4):
    g0: LineSegment StartX=-17.75 StartY=5 StartZ=0 EndX=71.9 EndY=5 EndZ=0
    g1: LineSegment StartX=71.9 StartY=5 StartZ=0 EndX=71.9 EndY=0 EndZ=0
    g2: LineSegment StartX=71.9 StartY=0 StartZ=0 EndX=-17.75 EndY=0 EndZ=0
    g3: LineSegment StartX=-17.75 StartY=0 StartZ=0 EndX=-17.75 EndY=5 EndZ=0
  constraints (12):
    c: Coincident(g0,g1)
    c: Coincident(g1,g2)
    c: Coincident(g2,g3)
    c: Coincident(g3,g0)
    c: Horizontal(g0)
    c: Horizontal(g2)
    c: Vertical(g1)
    c: Vertical(g3)
    c: PointOnObject(g1,g-1)
    c: DistanceY(g3,g3) = 5
    c: DistanceX(g2,g-1) = 17.75
    c: DistanceX(g-1,g1) = 71.9
FEATURE [PartDesign::Pocket] Pocket002  label="Pocket 2"
  BaseFeature = -> Pocket
  Direction = (0,1,-2e-16)
  Length = 25.6
  Length2 = 5
  Midplane = true
  Placement = pos=(0,0,0) rot=(1,0,0;1.5708rad)
  Profile = -> Sketch020
  ReferenceAxis = -> Sketch020 [N_Axis]
  Suppressed = false
  Type = 0
  expr: Length = 25 + 0.6
FEATURE [Sketcher::SketchObject] Sketch021
  ArcFitTolerance = 0
  AttachmentOffset = pos=(0,0,69.5) rot=(0,0,1;0rad)
  FullyConstrained = false
  MakeInternals = false
  MapMode = 5
  Placement = pos=(71.9,0,0) rot=(0.57735,0.57735,0.57735;2.0944rad)
  expr: .Placement.Base.x = Sketch018.Constraints.width
  expr: Constraints[9] = Sketch018.Constraints.MountingHeight / 2
  sketch-geometry (4):
    g0: Circle CenterX=-12.5 CenterY=97 CenterZ=0 NormalX=0 NormalY=0 NormalZ=1 AngleXU=0 Radius=1.77352
    g1: Circle CenterX=12.5 CenterY=97 CenterZ=0 NormalX=0 NormalY=0 NormalZ=1 AngleXU=0 Radius=1.77352
    g2: Circle CenterX=-12.5 CenterY=-5 CenterZ=0 NormalX=0 NormalY=0 NormalZ=1 AngleXU=0 Radius=1.77352
    g3: Circle CenterX=12.5 CenterY=-5 CenterZ=0 NormalX=0 NormalY=0 NormalZ=1 AngleXU=0 Radius=1.77352
  constraints (10):
    c: Symmetric(g0,g1,g-2)
    c: DistanceX(g0,g1) = 25
    c: Equal(g0,g1)
    c: DistanceY(g-1,g1) = 97
    c: Horizontal(g2,g3)
    c: Vertical(g0,g2)
    c: Vertical(g3,g1)
    c: Equal(g0,g2)
    c: Equal(g3,g2)
    c: DistanceY(g2,g-1) = 5
FEATURE [PartDesign::Hole] Hole006  label="Mounting holes"
  BaseFeature = -> Pocket002
  CustomThreadClearance = 0
  Depth = 320.149
  DepthType = 1
  Diameter = 5.3
  DrillForDepth = false
  DrillPoint = 1
  DrillPointAngle = 118
  HoleCutCountersinkAngle = 90
  HoleCutCustomValues = false
  HoleCutDepth = 5.4
  HoleCutDiameter = 8.9
  HoleCutType = 1
  ModelThread = false
  Placement = pos=(0,0,0) rot=(1,0,0;1.5708rad)
  Profile = -> Sketch021
  Reversed = true
  Suppressed = false
  Tapered = false
  TaperedAngle = 90
  ThreadClass = 0
  ThreadDepth = 320.149
  ThreadDepthType = 0
  ThreadDirection = 0
  ThreadFit = 0
  ThreadSize = 0
  ThreadType = 0
  Threaded = false
  UseCustomThreadClearance = false
FEATURE [Sketcher::SketchObject] Sketch022
  ArcFitTolerance = 0
  AttachmentOffset = pos=(0,0,62.5) rot=(0,0,1;0rad)
  FullyConstrained = true
  MakeInternals = false
  MapMode = 5
  Placement = pos=(62.5,0,0) rot=(0.57735,0.57735,0.57735;2.0944rad)
  expr: .Constraints.Width = 35 mm
  expr: .Constraints.magA = 20.2 mm + 0.2 mm * 2
  expr: .Constraints.magA2 = 4.2 mm + 0.2 mm * 2
  expr: Constraints[12] = 4.5 mm + 0.2 mm
  expr: Constraints[23] = 5 + 0.2
  expr: Constraints[57] = 0.75 * 3
  expr: Constraints[59] = 29.5 - 4.5
  expr: Constraints[60] = 84 - 8.25
  sketch-geometry (24):
    g0: LineSegment StartX=-17.5 StartY=225 StartZ=0 EndX=-17.5 EndY=4.7 EndZ=0
    g1: LineSegment StartX=-12.3 StartY=0 StartZ=0 EndX=12.3 EndY=0 EndZ=0
    g2: LineSegment StartX=17.5 StartY=4.7 StartZ=0 EndX=17.5 EndY=225 EndZ=0
    g3: LineSegment StartX=17.5 StartY=225 StartZ=0 EndX=-17.5 EndY=225 EndZ=0
    g4: GeomPoint [constr] X=0 Y=76.325 Z=0
    g5: LineSegment StartX=-12.3 StartY=4.7 StartZ=0 EndX=-12.3 EndY=0 EndZ=0
    g6: LineSegment StartX=12.3 StartY=0 StartZ=0 EndX=12.3 EndY=4.7 EndZ=0
    g7: LineSegment StartX=-17.5 StartY=4.7 StartZ=0 EndX=-12.3 EndY=4.7 EndZ=0
    g8: LineSegment StartX=12.3 StartY=4.7 StartZ=0 EndX=17.5 EndY=4.7 EndZ=0
    g9: ArcOfCircle CenterX=-8 CenterY=32.4 CenterZ=0 NormalX=0 NormalY=0 NormalZ=1 AngleXU=0 Radius=2.3 StartAngle=1.5708 EndAngle=4.71239
    g10: ArcOfCircle CenterX=8 CenterY=32.4 CenterZ=0 NormalX=0 NormalY=0 NormalZ=1 AngleXU=0 Radius=2.3 StartAngle=4.71239 EndAngle=7.85398
    g11: LineSegment StartX=-8 StartY=34.7 StartZ=0 EndX=8 EndY=34.7 EndZ=0
    g12: LineSegment StartX=-8 StartY=30.1 StartZ=0 EndX=8 EndY=30.1 EndZ=0
    g13: LineSegment [constr] StartX=-10.3 StartY=32.4 StartZ=0 EndX=10.3 EndY=32.4 EndZ=0
    g14: Circle CenterX=0 CenterY=20 CenterZ=0 NormalX=0 NormalY=0 NormalZ=1 AngleXU=0 Radius=7.5
    g15: LineSegment [constr] StartX=-12.5 StartY=38.45 StartZ=0 EndX=12.5 EndY=38.45 EndZ=0
    g16: LineSegment [constr] StartX=12.5 StartY=38.45 StartZ=0 EndX=12.5 EndY=114.2 EndZ=0
    g17: LineSegment [constr] StartX=12.5 StartY=114.2 StartZ=0 EndX=-12.5 EndY=114.2 EndZ=0
    g18: LineSegment [constr] StartX=-12.5 StartY=114.2 StartZ=0 EndX=-12.5 EndY=38.45 EndZ=0
    g19: GeomPoint [constr] X=0 Y=76.325 Z=0
    g20: Circle CenterX=-12.5 CenterY=114.2 CenterZ=0 NormalX=0 NormalY=0 NormalZ=1 AngleXU=0 Radius=1.125
    g21: Circle CenterX=12.5 CenterY=114.2 CenterZ=0 NormalX=0 NormalY=0 NormalZ=1 AngleXU=0 Radius=1.125
    g22: Circle CenterX=-12.5 CenterY=38.45 CenterZ=0 NormalX=0 NormalY=0 NormalZ=1 AngleXU=0 Radius=1.125
    g23: Circle CenterX=12.5 CenterY=38.45 CenterZ=0 NormalX=0 NormalY=0 NormalZ=1 AngleXU=0 Radius=1.125
  constraints (61):
    c: Coincident(g2,g3)
    c: Coincident(g3,g0)
    c: Vertical(g0)
    c: Vertical(g2)
    c: Horizontal(g1)
    c: Horizontal(g3)
    c: PointOnObject(g4,g-2)
    c: Vertical(g5)
    c: Vertical(g6)
    c: Coincident(g1,g5)
    c: Coincident(g1,g6)
    c: DistanceX(g0,g2) = 35  'Width'
    c: DistanceY(g6,g6) = 4.7
    c: PointOnObject(g-1,g1)
    c: Symmetric(g2,g0,g-2)
    c: DistanceY(g-1,g2) = 225  'height'
    c: Coincident(g7,g0)
    c: Horizontal(g7)
    c: Coincident(g8,g6)
    c: Coincident(g8,g2)
    c: Horizontal(g8)
    c: Equal(g7,g8)
    c: Coincident(g5,g7)
    c: DistanceX(g8,g8) = 5.2
    c: Tangent(g9,g11) = 1.5708
    c: Tangent(g9,g12) = -1.5708
    c: Tangent(g10,g11) = 1.5708
    c: Tangent(g10,g12) = -1.5708
    c: Equal(g9,g10)
    c: Symmetric(g10,g9,g-2)
    c: DistanceY(g9,g9) = 4.6  'magA2'
    c: Horizontal(g13)
    c: PointOnObject(g13,g9)
    c: PointOnObject(g13,g10)
    c: PointOnObject(g9,g13)
    c: DistanceX(g13,g13) = 20.6  'magA'
    c: DistanceY(g-1,g9) = 32.4  'magnetoffset'
    c: PointOnObject(g14,g-2)
    c: DistanceY(g-1,g14) = 20
    c: Diameter(g14) = 15
    c: Coincident(g15,g16)
    c: Coincident(g16,g17)
    c: Coincident(g17,g18)
    c: Coincident(g18,g15)
    c: Horizontal(g15)
    c: Horizontal(g17)
    c: Vertical(g16)
    c: Vertical(g18)
    c: Symmetric(g17,g15,g19)
    c: Coincident(g19,g4)
    c: Coincident(g20,g17)
    c: Coincident(g21,g16)
    c: Coincident(g22,g15)
    c: Coincident(g23,g15)
    c: Equal(g22,g23)
    c: Equal(g23,g21)
    c: Equal(g21,g20)
    c: Diameter(g20) = 2.25
    c: DistanceY(g-1,g17) = 114.2
    c: DistanceX(g17,g17) = 25
    c: DistanceY(g18,g18) = 75.75
FEATURE [PartDesign::Pad] Pad002  label="Pad All"
  Direction = (1,1e-16,-1e-16)
  Length = 9.4
  Length2 = 10
  Placement = pos=(62.5,0,0) rot=(0.57735,0.57735,0.57735;2.0944rad)
  Profile = -> Sketch022
  ReferenceAxis = -> Sketch022 [N_Axis]
  Refine = true
  Suppressed = false
  Type = 0
FEATURE [Sketcher::SketchObject] Sketch023
  ArcFitTolerance = 0
  AttachmentOffset = pos=(0,0,69.5) rot=(0,0,1;0rad)
  FullyConstrained = true
  MakeInternals = false
  MapMode = 5
  Placement = pos=(71.9,0,0) rot=(0.57735,0.57735,0.57735;2.0944rad)
  expr: .AttachmentOffset.Base.z = 62.5 mm + 7 mm
  expr: .Placement.Base.x = Sketch018.Constraints.width
  sketch-geometry (9):
    g0: LineSegment [constr] StartX=-12.5 StartY=10 StartZ=0 EndX=12.5 EndY=10 EndZ=0
    g1: LineSegment [constr] StartX=12.5 StartY=10 StartZ=0 EndX=12.5 EndY=25 EndZ=0
    g2: LineSegment [constr] StartX=12.5 StartY=25 StartZ=0 EndX=-12.5 EndY=25 EndZ=0
    g3: LineSegment [constr] StartX=-12.5 StartY=25 StartZ=0 EndX=-12.5 EndY=10 EndZ=0
    g4: GeomPoint [constr] X=0 Y=17.5 Z=0
    g5: Circle [constr] CenterX=-12.5 CenterY=25 CenterZ=0 NormalX=0 NormalY=0 NormalZ=1 AngleXU=0 Radius=2.5
    g6: Circle CenterX=-12.5 CenterY=10 CenterZ=0 NormalX=0 NormalY=0 NormalZ=1 AngleXU=0 Radius=2.5
    g7: Circle CenterX=12.5 CenterY=10 CenterZ=0 NormalX=0 NormalY=0 NormalZ=1 AngleXU=0 Radius=2.5
    g8: Circle [constr] CenterX=12.5 CenterY=25 CenterZ=0 NormalX=0 NormalY=0 NormalZ=1 AngleXU=0 Radius=2.5
  constraints (21):
    c: Coincident(g0,g1)
    c: Coincident(g1,g2)
    c: Coincident(g2,g3)
    c: Coincident(g3,g0)
    c: Horizontal(g0)
    c: Horizontal(g2)
    c: Vertical(g1)
    c: Vertical(g3)
    c: Symmetric(g2,g0,g4)
    c: PointOnObject(g4,g-2)
    c: DistanceX(g2,g2) = 25
    c: DistanceY(g1,g1) = 15
    c: DistanceY(g-1,g0) = 10
    c: Coincident(g5,g2)
    c: Coincident(g6,g0)
    c: Coincident(g7,g0)
    c: Coincident(g8,g1)
    c: Equal(g5,g6)
    c: Equal(g6,g7)
    c: Equal(g7,g8)
    c: Diameter(g8) = 5
FEATURE [PartDesign::Hole] Hole007  label="Hole mounting to nozzle"
  BaseFeature = -> Pad002
  CustomThreadClearance = 0
  Depth = 460.358
  DepthType = 1
  Diameter = 4
  DrillForDepth = false
  DrillPoint = 1
  DrillPointAngle = 118
  HoleCutCountersinkAngle = 90
  HoleCutCustomValues = false
  HoleCutDepth = 4.2
  HoleCutDiameter = 7.2
  HoleCutType = 1
  ModelThread = false
  Placement = pos=(62.5,0,0) rot=(0.57735,0.57735,0.57735;2.0944rad)
  Profile = -> Sketch023
  Refine = true
  Suppressed = false
  Tapered = false
  TaperedAngle = 90
  ThreadClass = 0
  ThreadDepth = 460.358
  ThreadDepthType = 0
  ThreadDirection = 0
  ThreadFit = 0
  ThreadSize = 0
  ThreadType = 0
  Threaded = false
  UseCustomThreadClearance = false
  expr: Diameter = 4
FEATURE [Mesh::Feature] Magnet_pogo_5pin  label="Magnet pogo 5pin male"
  Placement = pos=(71.9,0.1,32.3976) rot=(0.57735,-0.57735,-0.57735;2.0944rad)
  expr: .Placement.Base.x = Sketch018.Constraints.width
FEATURE [Mesh::Feature] Magnet_pogo_5pin_female  label="Magnet pogo 5pin female"
  Placement = pos=(69.8269,0.1,32.3924) rot=(0.57735,0.57735,0.57735;2.0944rad)
FEATURE [Sketcher::SketchObject] Sketch027
  ArcFitTolerance = 0
  AttachmentOffset = pos=(0,0,225) rot=(0,0,1;0rad)
  FullyConstrained = true
  MakeInternals = false
  MapMode = 5
  Placement = pos=(0,0,225) rot=(0,0,1;0rad)
  expr: .AttachmentOffset.Base.z = Sketch022.Constraints.height
  expr: Constraints[8] = 62.5 mm
  sketch-geometry (6):
    g0: ArcOfCircle CenterX=0 CenterY=0 CenterZ=0 NormalX=0 NormalY=0 NormalZ=1 AngleXU=0 Radius=47.5 StartAngle=5.89236 EndAngle=6.67401
    g1: ArcOfCircle CenterX=48.5412 CenterY=20 CenterZ=0 NormalX=0 NormalY=0 NormalZ=1 AngleXU=0 Radius=5 StartAngle=1.03324 EndAngle=3.53242
    g2: ArcOfCircle CenterX=48.5412 CenterY=-20 CenterZ=0 NormalX=0 NormalY=0 NormalZ=1 AngleXU=0 Radius=5 StartAngle=2.75077 EndAngle=5.24994
    g3: LineSegment StartX=62.5 StartY=17.5 StartZ=0 EndX=62.5 EndY=-17.5 EndZ=0
    g4: LineSegment StartX=62.5 StartY=-17.5 StartZ=0 EndX=51.1014 EndY=-24.2948 EndZ=0
    g5: LineSegment StartX=51.1014 StartY=24.2948 StartZ=0 EndX=62.5 EndY=17.5 EndZ=0
  constraints (15):
    c: Coincident(g0,g-1)
    c: Vertical(g1,g2)
    c: Equal(g1,g2)
    c: Radius(g0) = 47.5
    c: Tangent(g1,g0) = 1.5708
    c: Tangent(g2,g0) = 1.5708
    c: Symmetric(g3,g3,g-1)
    c: DistanceY(g3,g3) = 35
    c: DistanceX(g-1,g3) = 62.5
    c: DistanceY(g2,g1) = 40
    c: Coincident(g4,g3)
    c: Tangent(g4,g2) = 1.5708
    c: Coincident(g5,g3)
    c: Tangent(g5,g1) = 1.5708
    c: Radius(g1) = 5
FEATURE [Sketcher::SketchObject] Sketch028
  ArcFitTolerance = 0
  AttachmentOffset = pos=(0,0,205) rot=(0,0,1;0rad)
  FullyConstrained = true
  MakeInternals = false
  MapMode = 5
  Placement = pos=(0,0,205) rot=(0,0,1;0rad)
  expr: .AttachmentOffset.Base.z = Sketch022.Constraints.height - 20 mm
  sketch-geometry (4):
    g0: ArcOfCircle CenterX=0 CenterY=0 CenterZ=0 NormalX=0 NormalY=0 NormalZ=1 AngleXU=0 Radius=60 StartAngle=5.75959 EndAngle=6.80678
    g1: LineSegment StartX=51.9615 StartY=30 StartZ=0 EndX=62.5 EndY=30 EndZ=0
    g2: LineSegment StartX=62.5 StartY=30 StartZ=0 EndX=62.5 EndY=-30 EndZ=0
    g3: LineSegment StartX=62.5 StartY=-30 StartZ=0 EndX=51.9615 EndY=-30 EndZ=0
  constraints (11):
    c: Coincident(g0,g-1)
    c: Coincident(g1,g2)
    c: Coincident(g2,g3)
    c: Horizontal(g3)
    c: Coincident(g0,g1)
    c: Coincident(g0,g3)
    c: Symmetric(g1,g2,g-1)
    c: Horizontal(g1)
    c: Radius(g0) = 60
    c: DistanceX(g-1,g1) = 62.5
    c: DistanceY(g2,g2) = 60
FEATURE [Sketcher::SketchObject] Sketch029
  ArcFitTolerance = 0
  FullyConstrained = true
  MakeInternals = false
  MapMode = 5
  expr: Constraints[2] = 7.5
  sketch-geometry (1):
    g0: Circle CenterX=25 CenterY=7.5 CenterZ=0 NormalX=0 NormalY=0 NormalZ=1 AngleXU=0 Radius=2.75
  constraints (3):
    c: Diameter(g0) = 5.5
    c: DistanceX(g-1,g0) = 25
    c: DistanceY(g-1,g0) = 7.5
FEATURE [PartDesign::Pocket] Pocket007  label="Pocket air though hole"
  BaseFeature = -> Hole005
  Direction = (0,0,-1)
  Length = 5
  Length2 = 5
  Placement = pos=(0,0,0) rot=(1,0,0;1.5708rad)
  Profile = -> Sketch029
  ReferenceAxis = -> Sketch029 [N_Axis]
  Refine = true
  Reversed = true
  Suppressed = false
  Type = 1
FEATURE [PartDesign::Body] Body  label="Bottle Nozzle"
  AllowCompound = false
  Group = -> [Sketch,Revolution,Sketch003,Sketch005,Sketch006,Pad,Hole,Hole001,Sketch011,Hole002,Sketch012,Groove,Sketch013,Hole003,Sketch014,Hole004,Sketch015,Pocket001,Sketch016,Hole005,Sketch029,Pocket007]
  Origin = -> Origin
  Tip = -> Pocket007
FEATURE [Mesh::Feature] Coil_46_008_112  label="Coil 46.008.112"
  Placement = pos=(45,0,41.2) rot=(0,0,1;0rad)
FEATURE [Sketcher::SketchObject] Sketch030
  ArcFitTolerance = 0
  AttachmentOffset = pos=(0,0,62.5) rot=(0,0,1;0rad)
  FullyConstrained = true
  MakeInternals = false
  MapMode = 5
  Placement = pos=(62.5,0,0) rot=(0.57735,0.57735,0.57735;2.0944rad)
  expr: Constraints[11] = Sketch022.Constraints.Width
  expr: Constraints[7] = 30 - 0.2
  expr: Constraints[8] = 88 mm + 0.2 mm * 2
  sketch-geometry (4):
    g0: LineSegment StartX=-17.5 StartY=118.2 StartZ=0 EndX=-17.5 EndY=29.8 EndZ=0
    g1: LineSegment StartX=-17.5 StartY=29.8 StartZ=0 EndX=17.5 EndY=29.8 EndZ=0
    g2: LineSegment StartX=17.5 StartY=29.8 StartZ=0 EndX=17.5 EndY=118.2 EndZ=0
    g3: LineSegment StartX=17.5 StartY=118.2 StartZ=0 EndX=-17.5 EndY=118.2 EndZ=0
  constraints (12):
    c: Coincident(g0,g1)
    c: Coincident(g1,g2)
    c: Coincident(g2,g3)
    c: Coincident(g3,g0)
    c: Vertical(g0)
    c: Vertical(g2)
    c: Horizontal(g1)
    c: DistanceY(g-1,g1) = 29.8
    c: DistanceY(g0,g0) = 88.4
    c: DistanceY(g-1,g2) = 118.2  'PCBhieght'
    c: Symmetric(g0,g2,g-2)
    c: DistanceX(g3,g3) = 35
FEATURE [TechDraw::DrawSVGTemplate] Template
  Height = 210
  Orientation = 1
  Width = 297
FEATURE [TechDraw::DrawProjGroupItem] View
  CoarseView = false
  Direction = (0,-1,0)
  Focus = 100
  HardHidden = false
  IsoCount = 0
  IsoHidden = false
  IsoVisible = false
  LockPosition = false
  Perspective = false
  Rotation = 0
  RotationVector = (1,0,0)
  ScaleType = 0
  ScrubCount = 1
  SeamHidden = false
  SeamVisible = false
  SmoothHidden = false
  SmoothVisible = true
  Source = -> [Body]
  Type = 0
  X = 123.469
  XDirection = (1,0,0)
  Y = 88.6339
FEATURE [TechDraw::DrawProjGroupItem] View001
  CoarseView = false
  Direction = (1,3e-16,0)
  Focus = 100
  HardHidden = false
  IsoCount = 0
  IsoHidden = false
  IsoVisible = false
  LockPosition = false
  Perspective = false
  Rotation = 0
  RotationVector = (1,0,0)
  ScaleType = 0
  ScrubCount = 1
  SeamHidden = false
  SeamVisible = false
  SmoothHidden = false
  SmoothVisible = true
  Source = -> [Body]
  Type = 0
  X = 203.696
  XDirection = (-3e-16,1,0)
  Y = 88.6339
FEATURE [TechDraw::DrawProjGroupItem] View002
  CoarseView = false
  Direction = (0,0,1)
  Focus = 100
  HardHidden = false
  IsoCount = 0
  IsoHidden = false
  IsoVisible = false
  LockPosition = false
  Perspective = false
  Rotation = 0
  RotationVector = (1,0,0)
  ScaleType = 0
  ScrubCount = 1
  SeamHidden = false
  SeamVisible = false
  SmoothHidden = false
  SmoothVisible = true
  Source = -> [Body]
  Type = 0
  X = 123.469
  XDirection = (1,0,0)
  Y = 168.86
FEATURE [TechDraw::DrawViewDimension] Dimension
  AngleOverride = false
  Arbitrary = true
  ArbitraryTolerances = false
  EqualTolerance = true
  ExtensionAngle = 0
  FormatSpec = 4x M3
  FormatSpecOverTolerance = %+.2w
  FormatSpecUnderTolerance = %+.2w
  Inverted = false
  LineAngle = 0
  LockPosition = false
  MeasureType = 1
  OverTolerance = 0
  References2D = -> [View002]
  Rotation = 0
  ScaleType = 0
  TheoreticalExact = false
  Type = 5
  UnderTolerance = 0
  X = 56.3566
  Y = 21.4879
FEATURE [TechDraw::DrawViewDimension] Dimension001
  AngleOverride = false
  Arbitrary = true
  ArbitraryTolerances = false
  EqualTolerance = true
  ExtensionAngle = 0
  FormatSpec = 2x M4
  FormatSpecOverTolerance = %+.2w
  FormatSpecUnderTolerance = %+.2w
  Inverted = false
  LineAngle = 0
  LockPosition = false
  MeasureType = 1
  OverTolerance = 0
  References2D = -> [View001]
  Rotation = 0
  ScaleType = 0
  TheoreticalExact = false
  Type = 5
  UnderTolerance = 0
  X = 35.5629
  Y = -8.67711
FEATURE [TechDraw::DrawViewDimension] Dimension002
  AngleOverride = false
  Arbitrary = true
  ArbitraryTolerances = false
  EqualTolerance = true
  ExtensionAngle = 0
  FormatSpec = M8 10mm depth
  FormatSpecOverTolerance = %+.2w
  FormatSpecUnderTolerance = %+.2w
  Inverted = false
  LineAngle = 0
  LockPosition = false
  MeasureType = 1
  OverTolerance = 0
  References2D = -> [View001]
  Rotation = 0
  ScaleType = 0
  TheoreticalExact = false
  Type = 5
  UnderTolerance = 0
  X = 43.3565
  Y = 8.97265
FEATURE [TechDraw::DrawPage] Page  label="Bottle Nozzle threads"
  KeepUpdated = true
  NextBalloonIndex = 1
  ProjectionType = 0
  Template = -> Template
  Views = -> [View,View001,View002,Dimension,Dimension001,Dimension002]
FEATURE [Sketcher::SketchObject] Sketch026
  ArcFitTolerance = 0
  AttachmentOffset = pos=(0,0,62.5) rot=(0,0,1;0rad)
  FullyConstrained = true
  MakeInternals = false
  MapMode = 5
  Placement = pos=(69.9,0,0) rot=(0.57735,0.57735,0.57735;2.0944rad)
  expr: .AttachmentOffset.Base.z = 62.5 mm
  expr: .Constraints.magB = 25.9 + 0.2 * 2
  expr: .Constraints.magB2 = 4.3 mm + 0.2 mm * 2
  expr: Constraints[12] = Sketch022.Constraints.magnetoffset
  sketch-geometry (5):
    g0: ArcOfCircle CenterX=-10.8 CenterY=32.4 CenterZ=0 NormalX=0 NormalY=0 NormalZ=1 AngleXU=0 Radius=2.35 StartAngle=1.5708 EndAngle=4.71239
    g1: ArcOfCircle CenterX=10.8 CenterY=32.4 CenterZ=0 NormalX=0 NormalY=0 NormalZ=1 AngleXU=0 Radius=2.35 StartAngle=4.71239 EndAngle=7.85398
    g2: LineSegment StartX=-10.8 StartY=34.75 StartZ=0 EndX=10.8 EndY=34.75 EndZ=0
    g3: LineSegment StartX=-10.8 StartY=30.05 StartZ=0 EndX=10.8 EndY=30.05 EndZ=0
    g4: LineSegment [constr] StartX=-13.15 StartY=32.4 StartZ=0 EndX=13.15 EndY=32.4 EndZ=0
  constraints (13):
    c: Tangent(g0,g2) = 1.5708
    c: Tangent(g0,g3) = -1.5708
    c: Tangent(g1,g2) = 1.5708
    c: Tangent(g1,g3) = -1.5708
    c: Equal(g0,g1)
    c: Symmetric(g1,g0,g-2)
    c: DistanceY(g0,g0) = 4.7  'magB2'
    c: Horizontal(g4)
    c: PointOnObject(g4,g0)
    c: PointOnObject(g4,g1)
    c: PointOnObject(g1,g4)
    c: DistanceX(g4,g4) = 26.3  'magB'
    c: DistanceY(g-1,g4) = 32.4
FEATURE [PartDesign::Pocket] Pocket005  label="Pocket magnet"
  BaseFeature = -> Hole007
  Direction = (-1,-1e-16,1e-16)
  Length = 5
  Length2 = 5
  Placement = pos=(62.5,0,0) rot=(0.57735,0.57735,0.57735;2.0944rad)
  Profile = -> Sketch026
  ReferenceAxis = -> Sketch026 [N_Axis]
  Refine = true
  Suppressed = false
  Type = 0
FEATURE [PartDesign::Pad] Pad003  label="Pad bottle mount"
  BaseFeature = -> Pocket005
  Direction = (0,0,1)
  Length = 40
  Length2 = 10
  Placement = pos=(62.5,0,0) rot=(0.57735,0.57735,0.57735;2.0944rad)
  Profile = -> Sketch027
  ReferenceAxis = -> Sketch027 [N_Axis]
  Refine = true
  Reversed = true
  Suppressed = false
  Type = 0
  expr: Length = 40
FEATURE [PartDesign::Pocket] Pocket006  label="Pocket velcro hole"
  BaseFeature = -> Pad003
  Direction = (0,0,-1)
  Length = 25
  Length2 = 5
  Midplane = true
  Placement = pos=(62.5,0,0) rot=(0.57735,0.57735,0.57735;2.0944rad)
  Profile = -> Sketch028
  ReferenceAxis = -> Sketch028 [N_Axis]
  Refine = true
  Suppressed = false
  Type = 0
FEATURE [PartDesign::Pocket] Pocket008  label="Pocket PCB"
  BaseFeature = -> Pocket006
  Direction = (-1,-1e-16,1e-16)
  Length = 5.3
  Length2 = 5
  Placement = pos=(62.5,0,0) rot=(0.57735,0.57735,0.57735;2.0944rad)
  Profile = -> Sketch030
  ReferenceAxis = -> Sketch030 [N_Axis]
  Refine = true
  Reversed = true
  Suppressed = false
  Type = 0
FEATURE [Sketcher::SketchObject] Sketch031
  ArcFitTolerance = 0
  AttachmentOffset = pos=(0,0,62.5) rot=(0,0,1;0rad)
  FullyConstrained = false
  MakeInternals = false
  MapMode = 5
  Placement = pos=(62.5,0,0) rot=(0.57735,0.57735,0.57735;2.0944rad)
  sketch-geometry (12):
    g0: ArcOfCircle CenterX=12.7832 CenterY=107.278 CenterZ=0 NormalX=0 NormalY=0 NormalZ=1 AngleXU=0 Radius=1.06277 StartAngle=1e-16 EndAngle=3.14159
    g1: ArcOfCircle CenterX=12.7832 CenterY=84.0303 CenterZ=0 NormalX=0 NormalY=0 NormalZ=1 AngleXU=0 Radius=1.06277 StartAngle=3.14159 EndAngle=6.28319
    g2: LineSegment StartX=13.8459 StartY=107.278 StartZ=0 EndX=13.8459 EndY=84.0303 EndZ=0
    g3: LineSegment StartX=11.7204 StartY=107.278 StartZ=0 EndX=11.7204 EndY=84.0303 EndZ=0
    g4: ArcOfCircle CenterX=-13.3939 CenterY=108.813 CenterZ=0 NormalX=0 NormalY=0 NormalZ=1 AngleXU=0 Radius=1.06277 StartAngle=1.5708 EndAngle=4.71239
    g5: ArcOfCircle CenterX=6.99051 CenterY=108.813 CenterZ=0 NormalX=0 NormalY=0 NormalZ=1 AngleXU=0 Radius=1.06277 StartAngle=4.71239 EndAngle=7.85398
    g6: LineSegment StartX=-13.3939 StartY=109.876 StartZ=0 EndX=6.99051 EndY=109.876 EndZ=0
    g7: LineSegment StartX=-13.3939 StartY=107.75 StartZ=0 EndX=6.99051 EndY=107.75 EndZ=0
    g8: ArcOfCircle CenterX=-13.496 CenterY=93.656 CenterZ=0 NormalX=0 NormalY=0 NormalZ=1 AngleXU=0 Radius=1.06277 StartAngle=1.5708 EndAngle=4.71239
    g9: ArcOfCircle CenterX=6.96951 CenterY=93.656 CenterZ=0 NormalX=0 NormalY=0 NormalZ=1 AngleXU=0 Radius=1.06277 StartAngle=4.71239 EndAngle=7.85398
    g10: LineSegment StartX=-13.496 StartY=94.7188 StartZ=0 EndX=6.96951 EndY=94.7188 EndZ=0
    g11: LineSegment StartX=-13.496 StartY=92.5933 StartZ=0 EndX=6.96951 EndY=92.5933 EndZ=0
  constraints (20):
    c: Tangent(g0,g2) = 1.5708
    c: Tangent(g0,g3) = -1.5708
    c: Tangent(g1,g2) = 1.5708
    c: Tangent(g1,g3) = -1.5708
    c: Equal(g0,g1)
    c: Vertical(g2)
    c: Tangent(g4,g6) = 1.5708
    c: Tangent(g4,g7) = -1.5708
    c: Tangent(g5,g6) = 1.5708
    c: Tangent(g5,g7) = -1.5708
    c: Equal(g4,g5)
    c: Horizontal(g6)
    c: Tangent(g8,g10) = 1.5708
    c: Tangent(g8,g11) = -1.5708
    c: Tangent(g9,g10) = 1.5708
    c: Tangent(g9,g11) = -1.5708
    c: Equal(g8,g9)
    c: Horizontal(g10)
    c: Equal(g0,g5)
    c: Equal(g0,g9)
FEATURE [PartDesign::Pocket] Pocket009  label="Pocket THT"
  BaseFeature = -> Pocket008
  Direction = (-1,-1e-16,1e-16)
  Length = 8
  Length2 = 5
  Placement = pos=(62.5,0,0) rot=(0.57735,0.57735,0.57735;2.0944rad)
  Profile = -> Sketch031
  ReferenceAxis = -> Sketch031 [N_Axis]
  Refine = true
  Reversed = true
  Suppressed = false
  Type = 0
FEATURE [Sketcher::SketchObject] Sketch032
  ArcFitTolerance = 0
  AttachmentOffset = pos=(0,0,78.5) rot=(0,0,1;0rad)
  FullyConstrained = true
  MakeInternals = false
  MapMode = 5
  Placement = pos=(77.5,0,0) rot=(0.57735,0.57735,0.57735;2.0944rad)
  expr: .Placement.Base.x = Sketch018.Constraints.width + 5.6 mm
  sketch-geometry (4):
    g0: LineSegment StartX=-17.5 StartY=57.8 StartZ=0 EndX=-17.5 EndY=20.8 EndZ=0
    g1: LineSegment StartX=-17.5 StartY=20.8 StartZ=0 EndX=17.5 EndY=20.8 EndZ=0
    g2: LineSegment StartX=17.5 StartY=20.8 StartZ=0 EndX=17.5 EndY=57.8 EndZ=0
    g3: LineSegment StartX=17.5 StartY=57.8 StartZ=0 EndX=-17.5 EndY=57.8 EndZ=0
  constraints (11):
    c: Coincident(g0,g1)
    c: Coincident(g1,g2)
    c: Coincident(g2,g3)
    c: Coincident(g3,g0)
    c: Vertical(g0)
    c: Vertical(g2)
    c: Horizontal(g1)
    c: DistanceX(g3,g3) = 35
    c: DistanceY(g0,g0) = 37
    c: Symmetric(g0,g2,g-2)
    c: DistanceY(g-1,g0) = 20.8
FEATURE [PartDesign::Pocket] Pocket010  label="Pocket PCB slot"
  BaseFeature = -> Hole006
  Direction = (-1,-1e-16,1e-16)
  Length = 5
  Length2 = 5
  Placement = pos=(0,0,0) rot=(1,0,0;1.5708rad)
  Profile = -> Sketch032
  ReferenceAxis = -> Sketch032 [N_Axis]
  Refine = true
  Suppressed = false
  Type = 1
FEATURE [Sketcher::SketchObject] Sketch033
  ArcFitTolerance = 0
  FullyConstrained = true
  MakeInternals = false
  MapMode = 5
  Placement = pos=(0,0,0) rot=(1,0,0;1.5708rad)
  sketch-geometry (4):
    g0: LineSegment StartX=71.9 StartY=49 StartZ=0 EndX=71.9 EndY=34 EndZ=0
    g1: LineSegment StartX=71.9 StartY=34 StartZ=0 EndX=76.9 EndY=34 EndZ=0
    g2: LineSegment StartX=76.9 StartY=34 StartZ=0 EndX=76.9 EndY=49 EndZ=0
    g3: LineSegment StartX=76.9 StartY=49 StartZ=0 EndX=71.9 EndY=49 EndZ=0
  constraints (12):
    c: Coincident(g0,g1)
    c: Coincident(g1,g2)
    c: Coincident(g2,g3)
    c: Coincident(g3,g0)
    c: Vertical(g0)
    c: Vertical(g2)
    c: Horizontal(g1)
    c: Horizontal(g3)
    c: DistanceX(g-1,g0) = 71.9
    c: DistanceX(g1,g1) = 5
    c: DistanceY(g0,g0) = 15
    c: DistanceY(g-1,g0) = 34
FEATURE [PartDesign::Pocket] Pocket011  label="Pocket Connector"
  BaseFeature = -> Pocket010
  Direction = (0,1,-2e-16)
  Length = 5
  Length2 = 5
  Midplane = true
  Placement = pos=(0,0,0) rot=(1,0,0;1.5708rad)
  Profile = -> Sketch033
  ReferenceAxis = -> Sketch033 [N_Axis]
  Refine = true
  Suppressed = false
  Type = 1
FEATURE [Sketcher::SketchObject] Sketch034
  ArcFitTolerance = 0
  AttachmentOffset = pos=(0,0,80) rot=(0,0,1;0rad)
  FullyConstrained = false
  MakeInternals = false
  MapMode = 5
  Placement = pos=(80,0,0) rot=(0.57735,0.57735,0.57735;2.0944rad)
  expr: Constraints[35] = 2.54 * 4
  expr: Constraints[57] = 6 * 2.54
  sketch-geometry (27):
    g0: ArcOfCircle CenterX=-13.97 CenterY=46.66 CenterZ=0 NormalX=0 NormalY=0 NormalZ=1 AngleXU=0 Radius=1.75 StartAngle=3.7e-14 EndAngle=3.14159
    g1: ArcOfCircle CenterX=-13.97 CenterY=36.5 CenterZ=0 NormalX=0 NormalY=0 NormalZ=1 AngleXU=0 Radius=1.75 StartAngle=3.14159 EndAngle=6.28319
    g2: LineSegment StartX=-12.22 StartY=46.66 StartZ=0 EndX=-12.22 EndY=36.5 EndZ=0
    g3: LineSegment StartX=-15.72 StartY=46.66 StartZ=0 EndX=-15.72 EndY=36.5 EndZ=0
    g4: ArcOfCircle CenterX=13.97 CenterY=46.66 CenterZ=0 NormalX=0 NormalY=0 NormalZ=1 AngleXU=0 Radius=1.75 StartAngle=-9e-16 EndAngle=3.14159
    g5: ArcOfCircle CenterX=13.97 CenterY=36.5 CenterZ=0 NormalX=0 NormalY=0 NormalZ=1 AngleXU=0 Radius=1.75 StartAngle=3.14159 EndAngle=6.28319
    g6: LineSegment StartX=15.72 StartY=46.66 StartZ=0 EndX=15.72 EndY=36.5 EndZ=0
    g7: LineSegment StartX=12.22 StartY=46.66 StartZ=0 EndX=12.22 EndY=36.5 EndZ=0
    g8: LineSegment [constr] StartX=12.75 StartY=25.9438 StartZ=0 EndX=12.75 EndY=52.9438 EndZ=0
    g9: LineSegment [constr] StartX=12.75 StartY=52.9438 StartZ=0 EndX=-12.75 EndY=52.9438 EndZ=0
    g10: LineSegment [constr] StartX=-12.75 StartY=52.9438 StartZ=0 EndX=-12.75 EndY=25.9438 EndZ=0
    g11: LineSegment [constr] StartX=-12.75 StartY=25.9438 StartZ=0 EndX=12.75 EndY=25.9438 EndZ=0
    g12: GeomPoint [constr] X=1e-16 Y=39.4438 Z=0
    g13: Circle CenterX=-12.75 CenterY=52.9438 CenterZ=0 NormalX=0 NormalY=0 NormalZ=1 AngleXU=0 Radius=1.2
    g14: Circle CenterX=12.75 CenterY=52.9438 CenterZ=0 NormalX=0 NormalY=0 NormalZ=1 AngleXU=0 Radius=1.2
    g15: Circle CenterX=12.75 CenterY=25.9438 CenterZ=0 NormalX=0 NormalY=0 NormalZ=1 AngleXU=0 Radius=1.2
    g16: Circle CenterX=-12.75 CenterY=25.9438 CenterZ=0 NormalX=0 NormalY=0 NormalZ=1 AngleXU=0 Radius=1.2
    g17: LineSegment StartX=-7.62 StartY=46.66 StartZ=0 EndX=-7.62 EndY=32.3 EndZ=0
    g18: LineSegment StartX=-6.35 StartY=31.03 StartZ=0 EndX=6.35 EndY=31.03 EndZ=0
    g19: LineSegment StartX=7.62 StartY=32.3 StartZ=0 EndX=7.62 EndY=46.66 EndZ=0
    g20: LineSegment StartX=6.35 StartY=47.93 StartZ=0 EndX=-6.35 EndY=47.93 EndZ=0
    g21: ArcOfCircle CenterX=-6.35 CenterY=46.66 CenterZ=0 NormalX=0 NormalY=0 NormalZ=1 AngleXU=0 Radius=1.27 StartAngle=1.5708 EndAngle=3.14159
    g22: ArcOfCircle CenterX=-6.35 CenterY=32.3 CenterZ=0 NormalX=0 NormalY=0 NormalZ=1 AngleXU=0 Radius=1.27 StartAngle=3.14159 EndAngle=4.71239
    g23: ArcOfCircle CenterX=6.35 CenterY=32.3 CenterZ=0 NormalX=0 NormalY=0 NormalZ=1 AngleXU=0 Radius=1.27 StartAngle=4.71239 EndAngle=6.28319
    g24: ArcOfCircle CenterX=6.35 CenterY=46.66 CenterZ=0 NormalX=0 NormalY=0 NormalZ=1 AngleXU=0 Radius=1.27 StartAngle=3e-16 EndAngle=1.5708
    g25: GeomPoint [constr] X=-7.62 Y=47.93 Z=0
    g26: GeomPoint [constr] X=7.62 Y=31.03 Z=0
  constraints (60):
    c: Tangent(g0,g2) = 1.5708
    c: Tangent(g0,g3) = -1.5708
    c: Tangent(g1,g2) = 1.5708
    c: Tangent(g1,g3) = -1.5708
    c: Equal(g0,g1)
    c: Vertical(g2)
    c: Tangent(g4,g6) = 1.5708
    c: Tangent(g4,g7) = -1.5708
    c: Tangent(g5,g6) = 1.5708
    c: Tangent(g5,g7) = -1.5708
    c: Equal(g4,g5)
    c: Vertical(g6)
    c: Equal(g0,g4)
    c: Equal(g7,g2)
    c: Symmetric(g0,g4,g-2)
    c: Coincident(g8,g9)
    c: Coincident(g9,g10)
    c: Coincident(g10,g11)
    c: Coincident(g11,g8)
    c: Vertical(g8)
    c: Vertical(g10)
    c: Horizontal(g11)
    c: Symmetric(g10,g8,g12)
    c: Coincident(g13,g9)
    c: Coincident(g14,g8)
    c: Coincident(g15,g8)
    c: Coincident(g16,g10)
    c: Diameter(g13) = 2.4
    c: DistanceX(g9,g9) = 25.5
    c: DistanceY(g10,g10) = 27
    c: Equal(g13,g16)
    c: Equal(g16,g15)
    c: Equal(g15,g14)
    c: Symmetric(g9,g8,g-2)
    c: DistanceY(g-1,g1) = 36.5
    c: DistanceY(g1,g0) = 10.16
    c: DistanceX(g0,g4) = 27.94
    c: Radius(g0) = 1.75
    c: Tangent(g17,g21) = -1.5708
    c: Tangent(g17,g22) = -1.5708
    c: Tangent(g18,g22) = -1.5708
    c: Tangent(g18,g23) = -1.5708
    c: Tangent(g19,g23) = -1.5708
    c: Tangent(g19,g24) = -1.5708
    c: Tangent(g20,g24) = -1.5708
    c: Tangent(g20,g21) = -1.5708
    c: Vertical(g17)
    c: Vertical(g19)
    c: Horizontal(g18)
    c: Horizontal(g20)
    c: Equal(g21,g22)
    c: Equal(g23,g24)
    c: PointOnObject(g25,g17)
    c: PointOnObject(g25,g20)
    c: PointOnObject(g26,g18)
    c: PointOnObject(g26,g19)
    c: Symmetric(g22,g23,g-2)
    c: DistanceX(g17,g19) = 15.24
    c: DistanceY(g-1,g22) = 32.3
    c: Horizontal(g0,g21)
FEATURE [PartDesign::Pocket] Pocket012  label="Pocket PCB holes mount+THT"
  BaseFeature = -> Pocket011
  Direction = (-1,-1e-16,1e-16)
  Length = 5
  Length2 = 5
  Placement = pos=(0,0,0) rot=(1,0,0;1.5708rad)
  Profile = -> Sketch034
  ReferenceAxis = -> Sketch034 [N_Axis]
  Refine = true
  Suppressed = false
  Type = 1
FEATURE [PartDesign::Body] Body001  label="Wall Mount"
  AllowCompound = false
  Group = -> [Sketch018,Pad001,Sketch019,Pocket,Sketch020,Pocket002,Sketch021,Hole006,Sketch032,Pocket010,Sketch033,Pocket011,Sketch034,Pocket012]
  Origin = -> Origin001
  Tip = -> Pocket012
FEATURE [Sketcher::SketchObject] Sketch035
  ArcFitTolerance = 0
  FullyConstrained = true
  MakeInternals = false
  MapMode = 5
  Placement = pos=(0,0,0) rot=(1,0,0;1.5708rad)
  sketch-geometry (30):
    g0: LineSegment StartX=5.8 StartY=31.2 StartZ=0 EndX=6.7805 EndY=0 EndZ=0
    g1: LineSegment StartX=6.7805 StartY=0 StartZ=0 EndX=13.2 EndY=0 EndZ=0
    g2: LineSegment StartX=13.2 StartY=0 StartZ=0 EndX=13.2 EndY=2 EndZ=0
    g3: LineSegment StartX=13.2 StartY=2 StartZ=0 EndX=8.71765 EndY=2 EndZ=0
    g4: LineSegment StartX=8.71765 StartY=2 StartZ=0 EndX=8.57937 EndY=6.4 EndZ=0
    g5: LineSegment StartX=8.57937 StartY=6.4 StartZ=0 EndX=12.4 EndY=6.4 EndZ=0
    g6: LineSegment StartX=12.4 StartY=6.4 StartZ=0 EndX=12.4 EndY=8.4 EndZ=0
    g7: LineSegment StartX=12.4 StartY=8.4 StartZ=0 EndX=8.51652 EndY=8.4 EndZ=0
    g8: LineSegment StartX=8.51652 StartY=8.4 StartZ=0 EndX=8.45367 EndY=10.4 EndZ=0
    g9: LineSegment StartX=8.45367 StartY=10.4 StartZ=0 EndX=11.25 EndY=10.4 EndZ=0
    g10: LineSegment StartX=11.25 StartY=10.4 StartZ=0 EndX=11.25 EndY=12.4 EndZ=0
    g11: LineSegment StartX=11.25 StartY=12.4 StartZ=0 EndX=8.39081 EndY=12.4 EndZ=0
    g12: LineSegment StartX=8.39081 StartY=12.4 StartZ=0 EndX=8.32796 EndY=14.4 EndZ=0
    g13: LineSegment StartX=8.32796 StartY=14.4 StartZ=0 EndX=10.5 EndY=14.4 EndZ=0
    g14: LineSegment StartX=10.5 StartY=14.4 StartZ=0 EndX=10.5 EndY=16.4 EndZ=0
    g15: LineSegment StartX=10.5 StartY=16.4 StartZ=0 EndX=8.26511 EndY=16.4 EndZ=0
    g16: LineSegment StartX=8.26511 StartY=16.4 StartZ=0 EndX=8.17712 EndY=19.2 EndZ=0
    g17: LineSegment StartX=8.17712 StartY=19.2 StartZ=0 EndX=10.1 EndY=19.2 EndZ=0
    g18: LineSegment StartX=10.1 StartY=19.2 StartZ=0 EndX=10.1 EndY=20.4 EndZ=0
    g19: LineSegment StartX=10.1 StartY=20.4 StartZ=0 EndX=8.1394 EndY=20.4 EndZ=0
    g20: LineSegment StartX=8.1394 StartY=20.4 StartZ=0 EndX=8.05141 EndY=23.2 EndZ=0
    g21: LineSegment StartX=8.05141 StartY=23.2 StartZ=0 EndX=10.1 EndY=23.2 EndZ=0
    g22: LineSegment StartX=10.1 StartY=23.2 StartZ=0 EndX=10.1 EndY=24.4 EndZ=0
    g23: LineSegment StartX=10.1 StartY=24.4 StartZ=0 EndX=8.0137 EndY=24.4 EndZ=0
    g24: LineSegment StartX=8.0137 StartY=24.4 StartZ=0 EndX=7.92571 EndY=27.2 EndZ=0
    g25: LineSegment StartX=7.92571 StartY=27.2 StartZ=0 EndX=10.1 EndY=27.2 EndZ=0
    g26: LineSegment StartX=10.1 StartY=27.2 StartZ=0 EndX=10.1 EndY=28.4 EndZ=0
    g27: LineSegment StartX=10.1 StartY=28.4 StartZ=0 EndX=7.88799 EndY=28.4 EndZ=0
    g28: LineSegment StartX=7.88799 StartY=28.4 StartZ=0 EndX=7.8 EndY=31.2 EndZ=0
    g29: LineSegment StartX=7.8 StartY=31.2 StartZ=0 EndX=5.8 EndY=31.2 EndZ=0
  constraints (90):
    c: Coincident(g0,g1)
    c: Horizontal(g1)
    c: Coincident(g1,g2)
    c: Coincident(g2,g3)
    c: Horizontal(g3)
    c: Coincident(g3,g4)
    c: Coincident(g4,g5)
    c: Horizontal(g5)
    c: Coincident(g5,g6)
    c: Coincident(g6,g7)
    c: Horizontal(g7)
    c: Coincident(g7,g8)
    c: Coincident(g8,g9)
    c: Horizontal(g9)
    c: Coincident(g9,g10)
    c: Vertical(g10)
    c: Coincident(g10,g11)
    c: Horizontal(g11)
    c: Coincident(g11,g12)
    c: Coincident(g12,g13)
    c: Horizontal(g13)
    c: Coincident(g13,g14)
    c: Coincident(g14,g15)
    c: Horizontal(g15)
    c: Coincident(g15,g16)
    c: Coincident(g16,g17)
    c: Coincident(g17,g18)
    c: Coincident(g18,g19)
    c: Horizontal(g19)
    c: Coincident(g19,g20)
    c: Coincident(g20,g21)
    c: Horizontal(g21)
    c: Coincident(g21,g22)
    c: Coincident(g22,g23)
    c: Horizontal(g23)
    c: Coincident(g23,g24)
    c: Coincident(g24,g25)
    c: Horizontal(g25)
    c: Coincident(g25,g26)
    c: Vertical(g26)
    c: Coincident(g26,g27)
    c: Horizontal(g27)
    c: Coincident(g27,g28)
    c: Coincident(g28,g29)
    c: Coincident(g29,g0)
    c: Horizontal(g29)
    c: Angle(g-2,g0) = 0.0314159
    c: DistanceY(g0,g0) = 31.2
    c: DistanceX(g-1,g1) = 13.2
    c: Vertical(g2)
    c: Vertical(g14)
    c: Horizontal(g17)
    c: Vertical(g22)
    c: Vertical(g18)
    c: Vertical(g6)
    c: DistanceY(g2,g2) = 2
    c: Equal(g2,g6)
    c: Equal(g6,g10)
    c: Equal(g10,g14)
    c: DistanceY(g4,g4) = 4.4
    c: Equal(g8,g12)
    c: DistanceY(g8,g8) = 2
    c: DistanceY(g18,g18) = 1.2
    c: Equal(g26,g22)
    c: Equal(g22,g18)
    c: Equal(g16,g20)
    c: Equal(g20,g24)
    c: DistanceY(g16,g16) = 2.8
    c: Parallel(g0,g28)
    c: Parallel(g0,g24)
    c: Parallel(g20,g0)
    c: Parallel(g0,g16)
    c: Parallel(g0,g12)
    c: Parallel(g0,g8)
    c: Parallel(g0,g4)
    c: PointOnObject(g7,g4)
    c: PointOnObject(g11,g8)
    c: PointOnObject(g15,g12)
    c: PointOnObject(g19,g16)
    c: PointOnObject(g23,g20)
    c: PointOnObject(g27,g24)
    c: DistanceX(g29,g29) = 2
    c: DistanceX(g-1,g5) = 12.4
    c: DistanceX(g-1,g9) = 11.25
    c: DistanceX(g-1,g13) = 10.5
    c: DistanceX(g-1,g17) = 10.1
    c: PointOnObject(g21,g18)
    c: PointOnObject(g25,g22)
    c: PointOnObject(g-1,g1)
    c: DistanceX(g-1,g0) = 5.8
FEATURE [PartDesign::Revolution] Revolution001
  Angle = 360
  Angle2 = 60
  Axis = (0,2e-16,1)
  Base = (0,0,0)
  Placement = pos=(0,0,0) rot=(1,0,0;1.5708rad)
  Profile = -> Sketch035
  ReferenceAxis = -> Sketch035 [V_Axis]
  Refine = true
  Reversed = true
  Suppressed = false
  Type = 0
FEATURE [PartDesign::Body] Body003  label="Liquor pourer stopper"
  AllowCompound = false
  Group = -> [Sketch035,Revolution001]
  Origin = -> Origin003
  Placement = pos=(0,0,30.1095) rot=(0,0,1;0rad)
  Tip = -> Revolution001
FEATURE [Mesh::Feature] OBJ_PCB  label="PCB SLOT V2.2"
  Placement = pos=(74.93,-0.02,39.35) rot=(0.57735,-0.57735,-0.57735;2.0944rad)
FEATURE [Mesh::Feature] OBJ_PCB001  label="PCB Dispenser V2.003"
  Placement = pos=(61.8,0,74) rot=(0.57735,-0.57735,-0.57735;2.0944rad)
FEATURE [Part::FeaturePython] b_Air_Valve_WCD130_24B_001_  label="Air Valve WCD130-24B_001"  # a2plus imported part (geometry in sourceFile) (typed FeaturePython)
  Placement = pos=(57.2779,-0.0449,136.493) rot=(0,0.707107,0.707107;3.14159rad)
  a2p_Version = 0.4.68
  fixedPosition = true
  objectType = a2pPart
  sourceFile = ./../PreMade/Air Valve WCD130-24B.FCStd
  subassemblyImport = false
  timeLastImport = 1.74473e+09
  updateColors = true
FEATURE [Sketcher::SketchObject] Sketch039
  ArcFitTolerance = 1e-06
  AttachmentOffset = pos=(0,0,62.5) rot=(0,0,1;0rad)
  AttachmentSupport = -> [YZ_Plane002]
  FullyConstrained = true
  MakeInternals = false
  MapMode = 5
  Placement = pos=(62.5,0,0) rot=(0.57735,0.57735,0.57735;2.0944rad)
  expr: .AttachmentOffset.Base.z = 62.5 mm
  sketch-geometry (7):
    g0: LineSegment StartX=-10.5 StartY=136.25 StartZ=0 EndX=10.5 EndY=136.25 EndZ=0
    g1: LineSegment StartX=10.5 StartY=136.25 StartZ=0 EndX=10.5 EndY=167.75 EndZ=0
    g2: LineSegment StartX=10.5 StartY=167.75 StartZ=0 EndX=-10.5 EndY=167.75 EndZ=0
    g3: LineSegment StartX=-10.5 StartY=167.75 StartZ=0 EndX=-10.5 EndY=136.25 EndZ=0
    g4: GeomPoint [constr] X=0 Y=152 Z=0
    g5: LineSegment [constr] StartX=0 StartY=119 StartZ=0 EndX=-10.5 EndY=136.25 EndZ=0
    g6: LineSegment [constr] StartX=-10.5 StartY=167.75 StartZ=0 EndX=0 EndY=185 EndZ=0
  constraints (20):
    c: Coincident(g0,g1)
    c: Coincident(g1,g2)
    c: Coincident(g2,g3)
    c: Coincident(g3,g0)
    c: Horizontal(g0)
    c: Horizontal(g2)
    c: Vertical(g1)
    c: Vertical(g3)
    c: Symmetric(g2,g0,g4)
    c: DistanceY(g-1,g5) = 119
    c: Coincident(g5,g0)
    c: Coincident(g6,g2)
    c: Equal(g6,g5)
    c: DistanceY(g3,g3) = 31.5  'hh'
    c: DistanceX(g2,g2) = 21  'ww'
    c: PointOnObject(g4,g-2)
    c: DistanceY(g-1,g6) = 185
    c: PointOnObject(g5,g-2)
    c: PointOnObject(g6,g-2)
    c: DistanceY(g-1,g0) = 136.25  'height'
FEATURE [PartDesign::Pocket] Pocket013
  BaseFeature = -> Pocket009
  Direction = (-1,0,0)
  Length = 5
  Length2 = 5
  Placement = pos=(62.5,0,0) rot=(0.57735,0.57735,0.57735;2.0944rad)
  Profile = -> Sketch039
  ReferenceAxis = -> Sketch039 [N_Axis]
  Refine = true
  Reversed = true
  Suppressed = false
  Type = 0
FEATURE [Sketcher::SketchObject] Sketch040
  ArcFitTolerance = 1e-06
  AttachmentOffset = pos=(0,0,10.5) rot=(0,0,1;0rad)
  AttachmentSupport = -> [XZ_Plane002]
  FullyConstrained = false
  MakeInternals = false
  MapMode = 5
  Placement = pos=(0,-10.5,2.3e-15) rot=(1,0,0;1.5708rad)
  expr: .AttachmentOffset.Base.z = Sketch039.Constraints.ww / 2
  expr: Constraints[15] = Sketch039.Constraints.height
  expr: Constraints[16] = Sketch039.Constraints.hh
  sketch-geometry (8):
    g0: LineSegment StartX=62.5 StartY=167.75 StartZ=0 EndX=60 EndY=167.75 EndZ=0
    g1: LineSegment StartX=57.5 StartY=165.25 StartZ=0 EndX=57.5 EndY=138.75 EndZ=0
    g2: LineSegment StartX=60 StartY=136.25 StartZ=0 EndX=62.5 EndY=136.25 EndZ=0
    g3: ArcOfCircle CenterX=60 CenterY=165.25 CenterZ=0 NormalX=0 NormalY=0 NormalZ=1 AngleXU=0 Radius=2.5 StartAngle=1.5708 EndAngle=3.14159
    g4: ArcOfCircle CenterX=60 CenterY=138.75 CenterZ=0 NormalX=0 NormalY=0 NormalZ=1 AngleXU=0 Radius=2.5 StartAngle=3.14159 EndAngle=4.71239
    g5: GeomPoint [constr] X=69.6875 Y=136.25 Z=0
    g6: GeomPoint [constr] X=57.5 Y=167.75 Z=0
    g7: LineSegment StartX=62.5 StartY=136.25 StartZ=0 EndX=62.5 EndY=167.75 EndZ=0
  constraints (19):
    c: Tangent(g0,g3) = -1.5708
    c: Tangent(g1,g3) = -1.5708
    c: Tangent(g1,g4) = -1.5708
    c: Tangent(g2,g4) = -1.5708
    c: Vertical(g1)
    c: Horizontal(g0)
    c: Horizontal(g2)
    c: Equal(g3,g4)
    c: PointOnObject(g5,g2)
    c: PointOnObject(g6,g0)
    c: PointOnObject(g6,g1)
    c: Coincident(g7,g2)
    c: Coincident(g7,g0)
    c: Vertical(g7)
    c: DistanceX(g-1,g0) = 62.5
    c: DistanceY(g-1,g2) = 136.25
    c: DistanceY(g7,g7) = 31.5
    c: DistanceX(g1,g0) = 5
    c: Diameter(g4) = 5
FEATURE [PartDesign::Pad] Pad006  label="Pad air valve mount"
  BaseFeature = -> Pocket013
  Direction = (0,-1,2e-16)
  Length = 7
  Length2 = 10
  Placement = pos=(62.5,0,0) rot=(0.57735,0.57735,0.57735;2.0944rad)
  Profile = -> Sketch040
  ReferenceAxis = -> Sketch040 [N_Axis]
  Refine = true
  Suppressed = false
  Type = 0
FEATURE [Sketcher::SketchObject] Sketch041
  ArcFitTolerance = 1e-06
  AttachmentOffset = pos=(0,0,17.5) rot=(0,0,1;0rad)
  AttachmentSupport = -> [XZ_Plane002]
  FullyConstrained = false
  MakeInternals = false
  MapMode = 5
  Placement = pos=(0,-17.5,3.9e-15) rot=(1,0,0;1.5708rad)
  expr: .AttachmentOffset.Base.z = Sketch022.Constraints.Width / 2
  expr: Constraints[6] = Sketch039.Constraints.hh
  expr: Constraints[7] = Sketch039.Constraints.height
  sketch-geometry (4):
    g0: Circle CenterX=62.25 CenterY=159.5 CenterZ=0 NormalX=0 NormalY=0 NormalZ=1 AngleXU=0 Radius=3.59341
    g1: Circle CenterX=62.25 CenterY=144.5 CenterZ=0 NormalX=0 NormalY=0 NormalZ=1 AngleXU=0 Radius=3.25792
    g2: LineSegment [constr] StartX=62.25 StartY=159.5 StartZ=0 EndX=62.25 EndY=167.75 EndZ=0
    g3: LineSegment [constr] StartX=62.25 StartY=144.5 StartZ=0 EndX=62.25 EndY=136.25 EndZ=0
  constraints (10):
    c: DistanceY(g1,g0) = 15
    c: Coincident(g2,g0)
    c: Vertical(g2)
    c: Coincident(g3,g1)
    c: Vertical(g3)
    c: Equal(g2,g3)
    c: DistanceY(g3,g2) = 31.5
    c: DistanceY(g-1,g3) = 136.25
    c: Vertical(g0,g1)
    c: DistanceX(g-1,g2) = 62.25
FEATURE [PartDesign::Hole] Hole008  label="Hole air valve holder"
  BaseFeature = -> Pad006
  CustomThreadClearance = 0
  Depth = 20
  DepthType = 0
  Diameter = 3.3
  DrillForDepth = false
  DrillPoint = 1
  DrillPointAngle = 118
  HoleCutCountersinkAngle = 90
  HoleCutCustomValues = false
  HoleCutDepth = 4.5
  HoleCutDiameter = 5.7
  HoleCutType = 1
  ModelThread = false
  Placement = pos=(62.5,0,0) rot=(0.57735,0.57735,0.57735;2.0944rad)
  Profile = -> Sketch041
  Refine = true
  Suppressed = false
  Tapered = false
  TaperedAngle = 90
  ThreadClass = 0
  ThreadDepth = 20
  ThreadDepthType = 0
  ThreadDirection = 0
  ThreadFit = 0
  ThreadSize = 0
  ThreadType = 0
  Threaded = false
  UseCustomThreadClearance = false
  expr: Diameter = 3 + 0.3
  expr: HoleCutDepth = 7 - 2.5
  expr: HoleCutDiameter = 5.4 + 0.3
FEATURE [Sketcher::SketchObject] Sketch042
  ArcFitTolerance = 1e-06
  AttachmentOffset = pos=(0,0,67.7) rot=(0,0,1;0rad)
  AttachmentSupport = -> [YZ_Plane002]
  FullyConstrained = false
  MakeInternals = false
  MapMode = 5
  Placement = pos=(67.7,0,0) rot=(0.57735,0.57735,0.57735;2.0944rad)
  expr: .AttachmentOffset.Base.z = Sketch018.Constraints.width - 4.2 mm
  expr: Constraints[1] = Sketch022.Constraints.height - <<Pad bottle mount>>.Length / 2
  sketch-geometry (3):
    g0: Circle CenterX=-12.2676 CenterY=9.9453 CenterZ=0 NormalX=0 NormalY=0 NormalZ=1 AngleXU=0 Radius=4.84169
    g1: Circle CenterX=12.1343 CenterY=9.9453 CenterZ=0 NormalX=0 NormalY=0 NormalZ=1 AngleXU=0 Radius=4.91212
    g2: Circle CenterX=0 CenterY=205 CenterZ=0 NormalX=0 NormalY=0 NormalZ=1 AngleXU=0 Radius=5.95784
  constraints (2):
    c: PointOnObject(g2,g-2)
    c: DistanceY(g-1,g2) = 205
FEATURE [Sketcher::SketchObject] Sketch043
  ArcFitTolerance = 1e-06
  AttachmentOffset = pos=(0,0,71.9) rot=(0,0,1;0rad)
  AttachmentSupport = -> [YZ_Plane002]
  FullyConstrained = false
  MakeInternals = false
  MapMode = 5
  Placement = pos=(71.9,0,0) rot=(0.57735,0.57735,0.57735;2.0944rad)
  expr: .AttachmentOffset.Base.z = Sketch018.Constraints.width
  expr: Constraints[1] = Sketch022.Constraints.height - <<Pad bottle mount>>.Length / 2
  sketch-geometry (1):
    g0: Circle CenterX=0 CenterY=205 CenterZ=0 NormalX=0 NormalY=0 NormalZ=1 AngleXU=0 Radius=5.85773
  constraints (2):
    c: PointOnObject(g0,g-2)
    c: DistanceY(g-1,g0) = 205
FEATURE [PartDesign::Hole] Hole009  label="Hole Velcro holder"
  BaseFeature = -> Hole008
  CustomThreadClearance = 0
  Depth = 11
  DepthType = 0
  Diameter = 3.2
  DrillForDepth = false
  DrillPoint = 0
  DrillPointAngle = 118
  HoleCutCountersinkAngle = 90
  HoleCutCustomValues = false
  HoleCutDepth = 4.2
  HoleCutDiameter = 7.2
  HoleCutType = 1
  ModelThread = false
  Placement = pos=(62.5,0,0) rot=(0.57735,0.57735,0.57735;2.0944rad)
  Profile = -> Sketch043
  Refine = true
  Suppressed = false
  Tapered = false
  TaperedAngle = 83
  ThreadClass = 0
  ThreadDepth = 11
  ThreadDepthType = 0
  ThreadDirection = 0
  ThreadFit = 0
  ThreadSize = 0
  ThreadType = 0
  Threaded = false
  UseCustomThreadClearance = false
  expr: Diameter = 4 * 0.8
FEATURE [PartDesign::Pad] Pad007  label="Better printable"
  BaseFeature = -> Hole009
  Direction = (1,0,0)
  Length = 0.2
  Length2 = 10
  Placement = pos=(62.5,0,0) rot=(0.57735,0.57735,0.57735;2.0944rad)
  Profile = -> Sketch042
  ReferenceAxis = -> Sketch042 [N_Axis]
  Refine = true
  Suppressed = false
  Type = 0
FEATURE [PartDesign::Body] Body002  label="Bottle Holder"
  AllowCompound = false
  Group = -> [Sketch022,Pad002,Sketch023,Hole007,Sketch026,Pocket005,Sketch027,Pad003,Sketch028,Pocket006,Sketch030,Pocket008,Sketch031,Pocket009,Sketch039,Pocket013,Sketch040,Pad006,Sketch041,Hole008,Sketch042,Sketch043,Hole009,Pad007]
  Origin = -> Origin002
  Tip = -> Pad007
